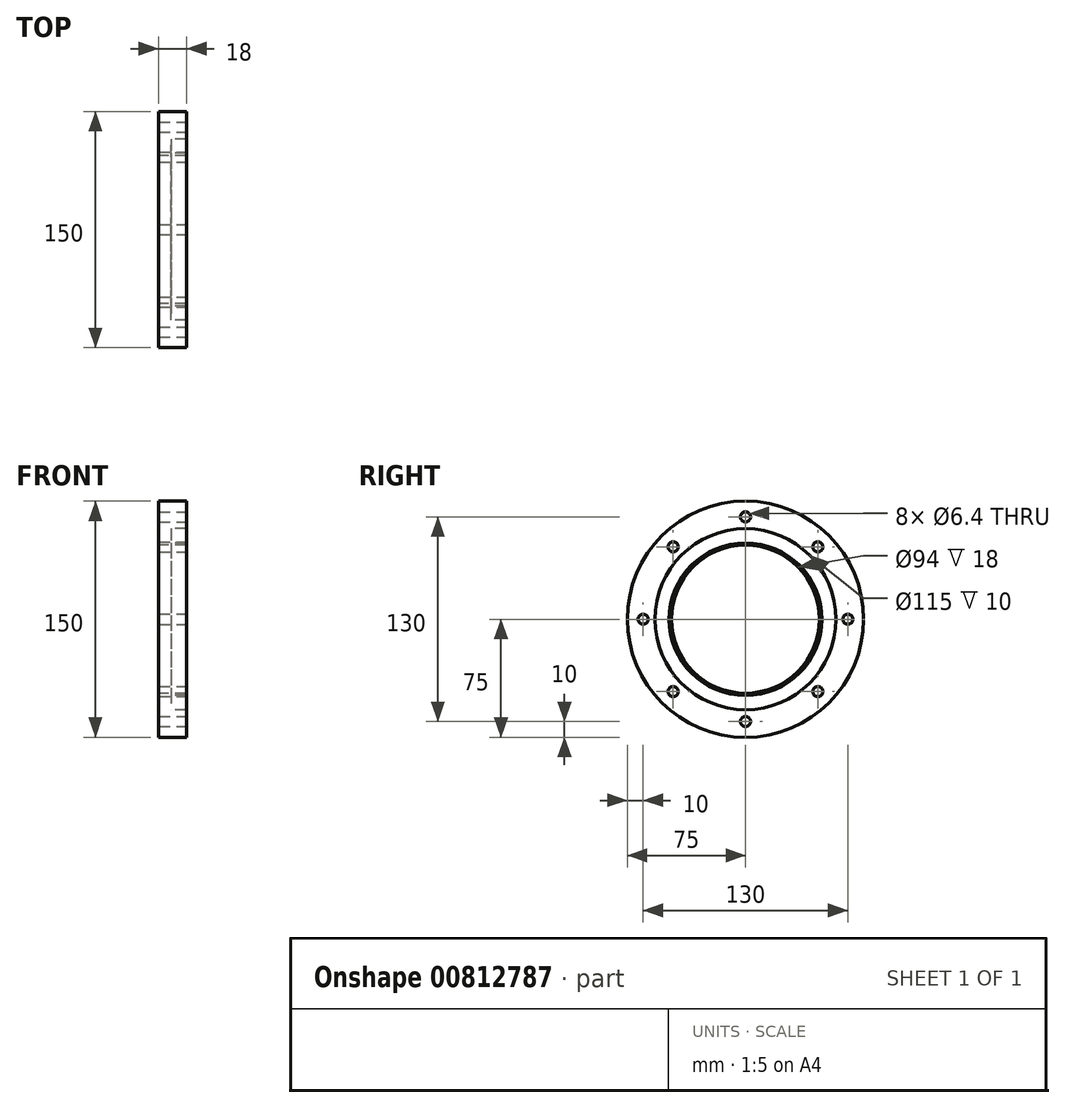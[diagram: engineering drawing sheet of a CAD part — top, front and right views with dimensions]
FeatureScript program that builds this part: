
annotation { "Feature Type Name" : "Feature", "Feature Type Description" : "" }
export const myFeature = defineFeature(function(context is Context, id is Id, definition is map)
    precondition{}
    {
        {
            assignVariable(context, id + "F0", {"name" : "meh", "anyValue" : 8});
        }
        {
            var Q0;
            Q0=qCreatedBy(makeId("Front.planeOp"),FACE);
            var sketch = newSketch(context, id + "F1", { "sketchPlane" : qUnion([Q0])});
            skLineSegment(sketch, "E0", {"start": v(0, 47) * mm, "end": v(0, 75) * mm});
            skLineSegment(sketch, "E1", {"start": v(0, 75) * mm, "end": v(18, 75) * mm});
            skLineSegment(sketch, "E2", {"start": v(18, 75) * mm, "end": v(18, 57.5) * mm});
            skLineSegment(sketch, "E3", {"start": v(18, 57.5) * mm, "end": v(8, 57.5) * mm});
            skLineSegment(sketch, "E4", {"start": v(8, 57.5) * mm, "end": v(8, 48.5) * mm});
            skLineSegment(sketch, "E5", {"start": v(8, 48.5) * mm, "end": v(18, 48.5) * mm});
            skLineSegment(sketch, "E6", {"start": v(18, 48.5) * mm, "end": v(18, 47) * mm});
            skLineSegment(sketch, "E7", {"start": v(18, 47) * mm, "end": v(0, 47) * mm});
            skLineSegment(sketch, "E8", {"start": v(0, 0) * mm, "end": v(18, 0) * mm, "construction": true});
            skSolve(sketch);
        }
        {
            var Q0;
            Q0 = qSketchRegion(id + "F1", true);
            var Q1;
            Q1=sQuery(id+"F1.wireOp",EDGE,"E8");
            revolve(context, id + "F2", {"surfaceOperationType" : NewSurfaceOperationType.NEW, "entities" : qUnion([Q0]), "axis" : qUnion([Q1]), "revolveType" : RevolveType.FULL});
        }
        {
            var Q0;
            Q0=makeQuery(id+"F2.opRevolve","SWEPT_FACE",FACE,{"disambiguationData":[OSD([sQuery(id+"F1.wireOp",EDGE,"E2")])]});
            var sketch = newSketch(context, id + "F3", { "sketchPlane" : qUnion([Q0])});
            skCircle(sketch, "E9", {"center": v(0, 65) * mm, "radius": 3.2 * mm});
            skSolve(sketch);
        }
        {
            var Q0;
            Q0 = qSketchRegion(id + "F3", true);
            var Q1;
            Q1=makeQuery(id+"F2.opRevolve","SWEPT_FACE",FACE,{"disambiguationData":[OSD([sQuery(id+"F1.wireOp",EDGE,"E0")])]});
            extrude(context, id + "F4", {"entities" : qUnion([Q0]), "endBound" : BoundingType.UP_TO_SURFACE, "oppositeDirection" : true, "depth" : 25 * mm, "endBoundEntityFace" : qUnion([Q1]), "offsetDistance" : 25 * mm});
        }
        {
            var Q0;
            Q0=makeQuery(id+"F4.opExtrude","SWEPT_BODY",BODY,{"disambiguationData":[OSD([sQuery(id+"F3.wireOp",EDGE,"E9")])]});
            var Q1;
            Q1=makeQuery(id+"F2.opRevolve","SWEPT_EDGE",EDGE,{"disambiguationData":[OSD([sQuery(id+"F1.wireOp",EDGE,"E1"),sQuery(id+"F1.wireOp",EDGE,"E2")])]});
            circularPattern(context, id + "F5", {"entities" : qUnion([Q0]), "axis" : qUnion([Q1]), "angle" : 360 * degree, "instanceCount" : getVariable(context, 'meh'), "equalSpace" : true});
        }
        {
            var Q0;
            Q0=makeQuery(id+"F4.opExtrude","SWEPT_BODY",BODY,{"disambiguationData":[OSD([sQuery(id+"F3.wireOp",EDGE,"E9")])]});
            var Q1;
            Q1=makeQuery(id+"F5.opPattern","COPY",BODY,{"derivedFrom":makeQuery(id+"F4.opExtrude","SWEPT_BODY",BODY,{"disambiguationData":[OSD([sQuery(id+"F3.wireOp",EDGE,"E9")])]}),"instanceName":"1"});
            var Q2;
            Q2=makeQuery(id+"F5.opPattern","COPY",BODY,{"derivedFrom":makeQuery(id+"F4.opExtrude","SWEPT_BODY",BODY,{"disambiguationData":[OSD([sQuery(id+"F3.wireOp",EDGE,"E9")])]}),"instanceName":"2"});
            var Q3;
            Q3=makeQuery(id+"F5.opPattern","COPY",BODY,{"derivedFrom":makeQuery(id+"F4.opExtrude","SWEPT_BODY",BODY,{"disambiguationData":[OSD([sQuery(id+"F3.wireOp",EDGE,"E9")])]}),"instanceName":"3"});
            var Q4;
            Q4=makeQuery(id+"F5.opPattern","COPY",BODY,{"derivedFrom":makeQuery(id+"F4.opExtrude","SWEPT_BODY",BODY,{"disambiguationData":[OSD([sQuery(id+"F3.wireOp",EDGE,"E9")])]}),"instanceName":"4"});
            var Q5;
            Q5=makeQuery(id+"F5.opPattern","COPY",BODY,{"derivedFrom":makeQuery(id+"F4.opExtrude","SWEPT_BODY",BODY,{"disambiguationData":[OSD([sQuery(id+"F3.wireOp",EDGE,"E9")])]}),"instanceName":"5"});
            var Q6;
            Q6=makeQuery(id+"F5.opPattern","COPY",BODY,{"derivedFrom":makeQuery(id+"F4.opExtrude","SWEPT_BODY",BODY,{"disambiguationData":[OSD([sQuery(id+"F3.wireOp",EDGE,"E9")])]}),"instanceName":"6"});
            var Q7;
            Q7=makeQuery(id+"F5.opPattern","COPY",BODY,{"derivedFrom":makeQuery(id+"F4.opExtrude","SWEPT_BODY",BODY,{"disambiguationData":[OSD([sQuery(id+"F3.wireOp",EDGE,"E9")])]}),"instanceName":"7"});
            var Q8;
            Q8=makeQuery(id+"F5.opPattern","COPY",BODY,{"derivedFrom":makeQuery(id+"F4.opExtrude","SWEPT_BODY",BODY,{"disambiguationData":[OSD([sQuery(id+"F3.wireOp",EDGE,"E9")])]}),"instanceName":"8"});
            var Q9;
            Q9=makeQuery(id+"F5.opPattern","COPY",BODY,{"derivedFrom":makeQuery(id+"F4.opExtrude","SWEPT_BODY",BODY,{"disambiguationData":[OSD([sQuery(id+"F3.wireOp",EDGE,"E9")])]}),"instanceName":"9"});
            var Q10;
            Q10=makeQuery(id+"F5.opPattern","COPY",BODY,{"derivedFrom":makeQuery(id+"F4.opExtrude","SWEPT_BODY",BODY,{"disambiguationData":[OSD([sQuery(id+"F3.wireOp",EDGE,"E9")])]}),"instanceName":"10"});
            var Q11;
            Q11=makeQuery(id+"F5.opPattern","COPY",BODY,{"derivedFrom":makeQuery(id+"F4.opExtrude","SWEPT_BODY",BODY,{"disambiguationData":[OSD([sQuery(id+"F3.wireOp",EDGE,"E9")])]}),"instanceName":"11"});
            var Q12;
            Q12=makeQuery(id+"F5.opPattern","COPY",BODY,{"derivedFrom":makeQuery(id+"F4.opExtrude","SWEPT_BODY",BODY,{"disambiguationData":[OSD([sQuery(id+"F3.wireOp",EDGE,"E9")])]}),"instanceName":"12"});
            var Q13;
            Q13=makeQuery(id+"F5.opPattern","COPY",BODY,{"derivedFrom":makeQuery(id+"F4.opExtrude","SWEPT_BODY",BODY,{"disambiguationData":[OSD([sQuery(id+"F3.wireOp",EDGE,"E9")])]}),"instanceName":"13"});
            var Q14;
            Q14=makeQuery(id+"F5.opPattern","COPY",BODY,{"derivedFrom":makeQuery(id+"F4.opExtrude","SWEPT_BODY",BODY,{"disambiguationData":[OSD([sQuery(id+"F3.wireOp",EDGE,"E9")])]}),"instanceName":"14"});
            var Q15;
            Q15=makeQuery(id+"F5.opPattern","COPY",BODY,{"derivedFrom":makeQuery(id+"F4.opExtrude","SWEPT_BODY",BODY,{"disambiguationData":[OSD([sQuery(id+"F3.wireOp",EDGE,"E9")])]}),"instanceName":"15"});
            var Q16;
            Q16=makeQuery(id+"F5.opPattern","COPY",BODY,{"derivedFrom":makeQuery(id+"F4.opExtrude","SWEPT_BODY",BODY,{"disambiguationData":[OSD([sQuery(id+"F3.wireOp",EDGE,"E9")])]}),"instanceName":"16"});
            var Q17;
            Q17=makeQuery(id+"F5.opPattern","COPY",BODY,{"derivedFrom":makeQuery(id+"F4.opExtrude","SWEPT_BODY",BODY,{"disambiguationData":[OSD([sQuery(id+"F3.wireOp",EDGE,"E9")])]}),"instanceName":"17"});
            var Q18;
            Q18=makeQuery(id+"F5.opPattern","COPY",BODY,{"derivedFrom":makeQuery(id+"F4.opExtrude","SWEPT_BODY",BODY,{"disambiguationData":[OSD([sQuery(id+"F3.wireOp",EDGE,"E9")])]}),"instanceName":"18"});
            var Q19;
            Q19=makeQuery(id+"F5.opPattern","COPY",BODY,{"derivedFrom":makeQuery(id+"F4.opExtrude","SWEPT_BODY",BODY,{"disambiguationData":[OSD([sQuery(id+"F3.wireOp",EDGE,"E9")])]}),"instanceName":"19"});
            var Q20;
            Q20=makeQuery(id+"F5.opPattern","COPY",BODY,{"derivedFrom":makeQuery(id+"F4.opExtrude","SWEPT_BODY",BODY,{"disambiguationData":[OSD([sQuery(id+"F3.wireOp",EDGE,"E9")])]}),"instanceName":"20"});
            var Q21;
            Q21=makeQuery(id+"F5.opPattern","COPY",BODY,{"derivedFrom":makeQuery(id+"F4.opExtrude","SWEPT_BODY",BODY,{"disambiguationData":[OSD([sQuery(id+"F3.wireOp",EDGE,"E9")])]}),"instanceName":"21"});
            var Q22;
            Q22=makeQuery(id+"F5.opPattern","COPY",BODY,{"derivedFrom":makeQuery(id+"F4.opExtrude","SWEPT_BODY",BODY,{"disambiguationData":[OSD([sQuery(id+"F3.wireOp",EDGE,"E9")])]}),"instanceName":"22"});
            var Q23;
            Q23=makeQuery(id+"F5.opPattern","COPY",BODY,{"derivedFrom":makeQuery(id+"F4.opExtrude","SWEPT_BODY",BODY,{"disambiguationData":[OSD([sQuery(id+"F3.wireOp",EDGE,"E9")])]}),"instanceName":"23"});
            var Q24;
            Q24=makeQuery(id+"F5.opPattern","COPY",BODY,{"derivedFrom":makeQuery(id+"F4.opExtrude","SWEPT_BODY",BODY,{"disambiguationData":[OSD([sQuery(id+"F3.wireOp",EDGE,"E9")])]}),"instanceName":"24"});
            var Q25;
            Q25=makeQuery(id+"F5.opPattern","COPY",BODY,{"derivedFrom":makeQuery(id+"F4.opExtrude","SWEPT_BODY",BODY,{"disambiguationData":[OSD([sQuery(id+"F3.wireOp",EDGE,"E9")])]}),"instanceName":"25"});
            var Q26;
            Q26=makeQuery(id+"F5.opPattern","COPY",BODY,{"derivedFrom":makeQuery(id+"F4.opExtrude","SWEPT_BODY",BODY,{"disambiguationData":[OSD([sQuery(id+"F3.wireOp",EDGE,"E9")])]}),"instanceName":"26"});
            var Q27;
            Q27=makeQuery(id+"F5.opPattern","COPY",BODY,{"derivedFrom":makeQuery(id+"F4.opExtrude","SWEPT_BODY",BODY,{"disambiguationData":[OSD([sQuery(id+"F3.wireOp",EDGE,"E9")])]}),"instanceName":"27"});
            var Q28;
            Q28=makeQuery(id+"F5.opPattern","COPY",BODY,{"derivedFrom":makeQuery(id+"F4.opExtrude","SWEPT_BODY",BODY,{"disambiguationData":[OSD([sQuery(id+"F3.wireOp",EDGE,"E9")])]}),"instanceName":"28"});
            var Q29;
            Q29=makeQuery(id+"F5.opPattern","COPY",BODY,{"derivedFrom":makeQuery(id+"F4.opExtrude","SWEPT_BODY",BODY,{"disambiguationData":[OSD([sQuery(id+"F3.wireOp",EDGE,"E9")])]}),"instanceName":"29"});
            var Q30;
            Q30=makeQuery(id+"F5.opPattern","COPY",BODY,{"derivedFrom":makeQuery(id+"F4.opExtrude","SWEPT_BODY",BODY,{"disambiguationData":[OSD([sQuery(id+"F3.wireOp",EDGE,"E9")])]}),"instanceName":"30"});
            var Q31;
            Q31=makeQuery(id+"F5.opPattern","COPY",BODY,{"derivedFrom":makeQuery(id+"F4.opExtrude","SWEPT_BODY",BODY,{"disambiguationData":[OSD([sQuery(id+"F3.wireOp",EDGE,"E9")])]}),"instanceName":"31"});
            var Q32;
            Q32=makeQuery(id+"F5.opPattern","COPY",BODY,{"derivedFrom":makeQuery(id+"F4.opExtrude","SWEPT_BODY",BODY,{"disambiguationData":[OSD([sQuery(id+"F3.wireOp",EDGE,"E9")])]}),"instanceName":"32"});
            var Q33;
            Q33=makeQuery(id+"F5.opPattern","COPY",BODY,{"derivedFrom":makeQuery(id+"F4.opExtrude","SWEPT_BODY",BODY,{"disambiguationData":[OSD([sQuery(id+"F3.wireOp",EDGE,"E9")])]}),"instanceName":"33"});
            var Q34;
            Q34=makeQuery(id+"F5.opPattern","COPY",BODY,{"derivedFrom":makeQuery(id+"F4.opExtrude","SWEPT_BODY",BODY,{"disambiguationData":[OSD([sQuery(id+"F3.wireOp",EDGE,"E9")])]}),"instanceName":"34"});
            var Q35;
            Q35=makeQuery(id+"F5.opPattern","COPY",BODY,{"derivedFrom":makeQuery(id+"F4.opExtrude","SWEPT_BODY",BODY,{"disambiguationData":[OSD([sQuery(id+"F3.wireOp",EDGE,"E9")])]}),"instanceName":"35"});
            var Q36;
            Q36=makeQuery(id+"F5.opPattern","COPY",BODY,{"derivedFrom":makeQuery(id+"F4.opExtrude","SWEPT_BODY",BODY,{"disambiguationData":[OSD([sQuery(id+"F3.wireOp",EDGE,"E9")])]}),"instanceName":"36"});
            var Q37;
            Q37=makeQuery(id+"F5.opPattern","COPY",BODY,{"derivedFrom":makeQuery(id+"F4.opExtrude","SWEPT_BODY",BODY,{"disambiguationData":[OSD([sQuery(id+"F3.wireOp",EDGE,"E9")])]}),"instanceName":"37"});
            var Q38;
            Q38=makeQuery(id+"F5.opPattern","COPY",BODY,{"derivedFrom":makeQuery(id+"F4.opExtrude","SWEPT_BODY",BODY,{"disambiguationData":[OSD([sQuery(id+"F3.wireOp",EDGE,"E9")])]}),"instanceName":"38"});
            var Q39;
            Q39=makeQuery(id+"F5.opPattern","COPY",BODY,{"derivedFrom":makeQuery(id+"F4.opExtrude","SWEPT_BODY",BODY,{"disambiguationData":[OSD([sQuery(id+"F3.wireOp",EDGE,"E9")])]}),"instanceName":"39"});
            var Q40;
            Q40=makeQuery(id+"F5.opPattern","COPY",BODY,{"derivedFrom":makeQuery(id+"F4.opExtrude","SWEPT_BODY",BODY,{"disambiguationData":[OSD([sQuery(id+"F3.wireOp",EDGE,"E9")])]}),"instanceName":"40"});
            var Q41;
            Q41=makeQuery(id+"F5.opPattern","COPY",BODY,{"derivedFrom":makeQuery(id+"F4.opExtrude","SWEPT_BODY",BODY,{"disambiguationData":[OSD([sQuery(id+"F3.wireOp",EDGE,"E9")])]}),"instanceName":"41"});
            var Q42;
            Q42=makeQuery(id+"F5.opPattern","COPY",BODY,{"derivedFrom":makeQuery(id+"F4.opExtrude","SWEPT_BODY",BODY,{"disambiguationData":[OSD([sQuery(id+"F3.wireOp",EDGE,"E9")])]}),"instanceName":"42"});
            var Q43;
            Q43=makeQuery(id+"F5.opPattern","COPY",BODY,{"derivedFrom":makeQuery(id+"F4.opExtrude","SWEPT_BODY",BODY,{"disambiguationData":[OSD([sQuery(id+"F3.wireOp",EDGE,"E9")])]}),"instanceName":"43"});
            var Q44;
            Q44=makeQuery(id+"F5.opPattern","COPY",BODY,{"derivedFrom":makeQuery(id+"F4.opExtrude","SWEPT_BODY",BODY,{"disambiguationData":[OSD([sQuery(id+"F3.wireOp",EDGE,"E9")])]}),"instanceName":"44"});
            var Q45;
            Q45=makeQuery(id+"F5.opPattern","COPY",BODY,{"derivedFrom":makeQuery(id+"F4.opExtrude","SWEPT_BODY",BODY,{"disambiguationData":[OSD([sQuery(id+"F3.wireOp",EDGE,"E9")])]}),"instanceName":"45"});
            var Q46;
            Q46=makeQuery(id+"F5.opPattern","COPY",BODY,{"derivedFrom":makeQuery(id+"F4.opExtrude","SWEPT_BODY",BODY,{"disambiguationData":[OSD([sQuery(id+"F3.wireOp",EDGE,"E9")])]}),"instanceName":"46"});
            var Q47;
            Q47=makeQuery(id+"F5.opPattern","COPY",BODY,{"derivedFrom":makeQuery(id+"F4.opExtrude","SWEPT_BODY",BODY,{"disambiguationData":[OSD([sQuery(id+"F3.wireOp",EDGE,"E9")])]}),"instanceName":"47"});
            var Q48;
            Q48=makeQuery(id+"F5.opPattern","COPY",BODY,{"derivedFrom":makeQuery(id+"F4.opExtrude","SWEPT_BODY",BODY,{"disambiguationData":[OSD([sQuery(id+"F3.wireOp",EDGE,"E9")])]}),"instanceName":"48"});
            var Q49;
            Q49=makeQuery(id+"F5.opPattern","COPY",BODY,{"derivedFrom":makeQuery(id+"F4.opExtrude","SWEPT_BODY",BODY,{"disambiguationData":[OSD([sQuery(id+"F3.wireOp",EDGE,"E9")])]}),"instanceName":"49"});
            var Q50;
            Q50=makeQuery(id+"F5.opPattern","COPY",BODY,{"derivedFrom":makeQuery(id+"F4.opExtrude","SWEPT_BODY",BODY,{"disambiguationData":[OSD([sQuery(id+"F3.wireOp",EDGE,"E9")])]}),"instanceName":"50"});
            var Q51;
            Q51=makeQuery(id+"F5.opPattern","COPY",BODY,{"derivedFrom":makeQuery(id+"F4.opExtrude","SWEPT_BODY",BODY,{"disambiguationData":[OSD([sQuery(id+"F3.wireOp",EDGE,"E9")])]}),"instanceName":"51"});
            var Q52;
            Q52=makeQuery(id+"F5.opPattern","COPY",BODY,{"derivedFrom":makeQuery(id+"F4.opExtrude","SWEPT_BODY",BODY,{"disambiguationData":[OSD([sQuery(id+"F3.wireOp",EDGE,"E9")])]}),"instanceName":"52"});
            var Q53;
            Q53=makeQuery(id+"F5.opPattern","COPY",BODY,{"derivedFrom":makeQuery(id+"F4.opExtrude","SWEPT_BODY",BODY,{"disambiguationData":[OSD([sQuery(id+"F3.wireOp",EDGE,"E9")])]}),"instanceName":"53"});
            var Q54;
            Q54=makeQuery(id+"F5.opPattern","COPY",BODY,{"derivedFrom":makeQuery(id+"F4.opExtrude","SWEPT_BODY",BODY,{"disambiguationData":[OSD([sQuery(id+"F3.wireOp",EDGE,"E9")])]}),"instanceName":"54"});
            var Q55;
            Q55=makeQuery(id+"F5.opPattern","COPY",BODY,{"derivedFrom":makeQuery(id+"F4.opExtrude","SWEPT_BODY",BODY,{"disambiguationData":[OSD([sQuery(id+"F3.wireOp",EDGE,"E9")])]}),"instanceName":"55"});
            var Q56;
            Q56=makeQuery(id+"F5.opPattern","COPY",BODY,{"derivedFrom":makeQuery(id+"F4.opExtrude","SWEPT_BODY",BODY,{"disambiguationData":[OSD([sQuery(id+"F3.wireOp",EDGE,"E9")])]}),"instanceName":"56"});
            var Q57;
            Q57=makeQuery(id+"F5.opPattern","COPY",BODY,{"derivedFrom":makeQuery(id+"F4.opExtrude","SWEPT_BODY",BODY,{"disambiguationData":[OSD([sQuery(id+"F3.wireOp",EDGE,"E9")])]}),"instanceName":"57"});
            var Q58;
            Q58=makeQuery(id+"F5.opPattern","COPY",BODY,{"derivedFrom":makeQuery(id+"F4.opExtrude","SWEPT_BODY",BODY,{"disambiguationData":[OSD([sQuery(id+"F3.wireOp",EDGE,"E9")])]}),"instanceName":"58"});
            var Q59;
            Q59=makeQuery(id+"F5.opPattern","COPY",BODY,{"derivedFrom":makeQuery(id+"F4.opExtrude","SWEPT_BODY",BODY,{"disambiguationData":[OSD([sQuery(id+"F3.wireOp",EDGE,"E9")])]}),"instanceName":"59"});
            var Q60;
            Q60=makeQuery(id+"F5.opPattern","COPY",BODY,{"derivedFrom":makeQuery(id+"F4.opExtrude","SWEPT_BODY",BODY,{"disambiguationData":[OSD([sQuery(id+"F3.wireOp",EDGE,"E9")])]}),"instanceName":"60"});
            var Q61;
            Q61=makeQuery(id+"F5.opPattern","COPY",BODY,{"derivedFrom":makeQuery(id+"F4.opExtrude","SWEPT_BODY",BODY,{"disambiguationData":[OSD([sQuery(id+"F3.wireOp",EDGE,"E9")])]}),"instanceName":"61"});
            var Q62;
            Q62=makeQuery(id+"F5.opPattern","COPY",BODY,{"derivedFrom":makeQuery(id+"F4.opExtrude","SWEPT_BODY",BODY,{"disambiguationData":[OSD([sQuery(id+"F3.wireOp",EDGE,"E9")])]}),"instanceName":"62"});
            var Q63;
            Q63=makeQuery(id+"F5.opPattern","COPY",BODY,{"derivedFrom":makeQuery(id+"F4.opExtrude","SWEPT_BODY",BODY,{"disambiguationData":[OSD([sQuery(id+"F3.wireOp",EDGE,"E9")])]}),"instanceName":"63"});
            var Q64;
            Q64=makeQuery(id+"F5.opPattern","COPY",BODY,{"derivedFrom":makeQuery(id+"F4.opExtrude","SWEPT_BODY",BODY,{"disambiguationData":[OSD([sQuery(id+"F3.wireOp",EDGE,"E9")])]}),"instanceName":"64"});
            var Q65;
            Q65=makeQuery(id+"F5.opPattern","COPY",BODY,{"derivedFrom":makeQuery(id+"F4.opExtrude","SWEPT_BODY",BODY,{"disambiguationData":[OSD([sQuery(id+"F3.wireOp",EDGE,"E9")])]}),"instanceName":"65"});
            var Q66;
            Q66=makeQuery(id+"F5.opPattern","COPY",BODY,{"derivedFrom":makeQuery(id+"F4.opExtrude","SWEPT_BODY",BODY,{"disambiguationData":[OSD([sQuery(id+"F3.wireOp",EDGE,"E9")])]}),"instanceName":"66"});
            var Q67;
            Q67=makeQuery(id+"F5.opPattern","COPY",BODY,{"derivedFrom":makeQuery(id+"F4.opExtrude","SWEPT_BODY",BODY,{"disambiguationData":[OSD([sQuery(id+"F3.wireOp",EDGE,"E9")])]}),"instanceName":"67"});
            var Q68;
            Q68=makeQuery(id+"F5.opPattern","COPY",BODY,{"derivedFrom":makeQuery(id+"F4.opExtrude","SWEPT_BODY",BODY,{"disambiguationData":[OSD([sQuery(id+"F3.wireOp",EDGE,"E9")])]}),"instanceName":"68"});
            var Q69;
            Q69=makeQuery(id+"F5.opPattern","COPY",BODY,{"derivedFrom":makeQuery(id+"F4.opExtrude","SWEPT_BODY",BODY,{"disambiguationData":[OSD([sQuery(id+"F3.wireOp",EDGE,"E9")])]}),"instanceName":"69"});
            var Q70;
            Q70=makeQuery(id+"F5.opPattern","COPY",BODY,{"derivedFrom":makeQuery(id+"F4.opExtrude","SWEPT_BODY",BODY,{"disambiguationData":[OSD([sQuery(id+"F3.wireOp",EDGE,"E9")])]}),"instanceName":"70"});
            var Q71;
            Q71=makeQuery(id+"F5.opPattern","COPY",BODY,{"derivedFrom":makeQuery(id+"F4.opExtrude","SWEPT_BODY",BODY,{"disambiguationData":[OSD([sQuery(id+"F3.wireOp",EDGE,"E9")])]}),"instanceName":"71"});
            var Q72;
            Q72=makeQuery(id+"F5.opPattern","COPY",BODY,{"derivedFrom":makeQuery(id+"F4.opExtrude","SWEPT_BODY",BODY,{"disambiguationData":[OSD([sQuery(id+"F3.wireOp",EDGE,"E9")])]}),"instanceName":"72"});
            var Q73;
            Q73=makeQuery(id+"F5.opPattern","COPY",BODY,{"derivedFrom":makeQuery(id+"F4.opExtrude","SWEPT_BODY",BODY,{"disambiguationData":[OSD([sQuery(id+"F3.wireOp",EDGE,"E9")])]}),"instanceName":"73"});
            var Q74;
            Q74=makeQuery(id+"F5.opPattern","COPY",BODY,{"derivedFrom":makeQuery(id+"F4.opExtrude","SWEPT_BODY",BODY,{"disambiguationData":[OSD([sQuery(id+"F3.wireOp",EDGE,"E9")])]}),"instanceName":"74"});
            var Q75;
            Q75=makeQuery(id+"F5.opPattern","COPY",BODY,{"derivedFrom":makeQuery(id+"F4.opExtrude","SWEPT_BODY",BODY,{"disambiguationData":[OSD([sQuery(id+"F3.wireOp",EDGE,"E9")])]}),"instanceName":"75"});
            var Q76;
            Q76=makeQuery(id+"F5.opPattern","COPY",BODY,{"derivedFrom":makeQuery(id+"F4.opExtrude","SWEPT_BODY",BODY,{"disambiguationData":[OSD([sQuery(id+"F3.wireOp",EDGE,"E9")])]}),"instanceName":"76"});
            var Q77;
            Q77=makeQuery(id+"F5.opPattern","COPY",BODY,{"derivedFrom":makeQuery(id+"F4.opExtrude","SWEPT_BODY",BODY,{"disambiguationData":[OSD([sQuery(id+"F3.wireOp",EDGE,"E9")])]}),"instanceName":"77"});
            var Q78;
            Q78=makeQuery(id+"F5.opPattern","COPY",BODY,{"derivedFrom":makeQuery(id+"F4.opExtrude","SWEPT_BODY",BODY,{"disambiguationData":[OSD([sQuery(id+"F3.wireOp",EDGE,"E9")])]}),"instanceName":"78"});
            var Q79;
            Q79=makeQuery(id+"F5.opPattern","COPY",BODY,{"derivedFrom":makeQuery(id+"F4.opExtrude","SWEPT_BODY",BODY,{"disambiguationData":[OSD([sQuery(id+"F3.wireOp",EDGE,"E9")])]}),"instanceName":"79"});
            var Q80;
            Q80=makeQuery(id+"F5.opPattern","COPY",BODY,{"derivedFrom":makeQuery(id+"F4.opExtrude","SWEPT_BODY",BODY,{"disambiguationData":[OSD([sQuery(id+"F3.wireOp",EDGE,"E9")])]}),"instanceName":"80"});
            var Q81;
            Q81=makeQuery(id+"F5.opPattern","COPY",BODY,{"derivedFrom":makeQuery(id+"F4.opExtrude","SWEPT_BODY",BODY,{"disambiguationData":[OSD([sQuery(id+"F3.wireOp",EDGE,"E9")])]}),"instanceName":"81"});
            var Q82;
            Q82=makeQuery(id+"F5.opPattern","COPY",BODY,{"derivedFrom":makeQuery(id+"F4.opExtrude","SWEPT_BODY",BODY,{"disambiguationData":[OSD([sQuery(id+"F3.wireOp",EDGE,"E9")])]}),"instanceName":"82"});
            var Q83;
            Q83=makeQuery(id+"F5.opPattern","COPY",BODY,{"derivedFrom":makeQuery(id+"F4.opExtrude","SWEPT_BODY",BODY,{"disambiguationData":[OSD([sQuery(id+"F3.wireOp",EDGE,"E9")])]}),"instanceName":"83"});
            var Q84;
            Q84=makeQuery(id+"F5.opPattern","COPY",BODY,{"derivedFrom":makeQuery(id+"F4.opExtrude","SWEPT_BODY",BODY,{"disambiguationData":[OSD([sQuery(id+"F3.wireOp",EDGE,"E9")])]}),"instanceName":"84"});
            var Q85;
            Q85=makeQuery(id+"F5.opPattern","COPY",BODY,{"derivedFrom":makeQuery(id+"F4.opExtrude","SWEPT_BODY",BODY,{"disambiguationData":[OSD([sQuery(id+"F3.wireOp",EDGE,"E9")])]}),"instanceName":"85"});
            var Q86;
            Q86=makeQuery(id+"F5.opPattern","COPY",BODY,{"derivedFrom":makeQuery(id+"F4.opExtrude","SWEPT_BODY",BODY,{"disambiguationData":[OSD([sQuery(id+"F3.wireOp",EDGE,"E9")])]}),"instanceName":"86"});
            var Q87;
            Q87=makeQuery(id+"F5.opPattern","COPY",BODY,{"derivedFrom":makeQuery(id+"F4.opExtrude","SWEPT_BODY",BODY,{"disambiguationData":[OSD([sQuery(id+"F3.wireOp",EDGE,"E9")])]}),"instanceName":"87"});
            var Q88;
            Q88=makeQuery(id+"F5.opPattern","COPY",BODY,{"derivedFrom":makeQuery(id+"F4.opExtrude","SWEPT_BODY",BODY,{"disambiguationData":[OSD([sQuery(id+"F3.wireOp",EDGE,"E9")])]}),"instanceName":"88"});
            var Q89;
            Q89=makeQuery(id+"F5.opPattern","COPY",BODY,{"derivedFrom":makeQuery(id+"F4.opExtrude","SWEPT_BODY",BODY,{"disambiguationData":[OSD([sQuery(id+"F3.wireOp",EDGE,"E9")])]}),"instanceName":"89"});
            var Q90;
            Q90=makeQuery(id+"F5.opPattern","COPY",BODY,{"derivedFrom":makeQuery(id+"F4.opExtrude","SWEPT_BODY",BODY,{"disambiguationData":[OSD([sQuery(id+"F3.wireOp",EDGE,"E9")])]}),"instanceName":"90"});
            var Q91;
            Q91=makeQuery(id+"F5.opPattern","COPY",BODY,{"derivedFrom":makeQuery(id+"F4.opExtrude","SWEPT_BODY",BODY,{"disambiguationData":[OSD([sQuery(id+"F3.wireOp",EDGE,"E9")])]}),"instanceName":"91"});
            var Q92;
            Q92=makeQuery(id+"F5.opPattern","COPY",BODY,{"derivedFrom":makeQuery(id+"F4.opExtrude","SWEPT_BODY",BODY,{"disambiguationData":[OSD([sQuery(id+"F3.wireOp",EDGE,"E9")])]}),"instanceName":"92"});
            var Q93;
            Q93=makeQuery(id+"F5.opPattern","COPY",BODY,{"derivedFrom":makeQuery(id+"F4.opExtrude","SWEPT_BODY",BODY,{"disambiguationData":[OSD([sQuery(id+"F3.wireOp",EDGE,"E9")])]}),"instanceName":"93"});
            var Q94;
            Q94=makeQuery(id+"F5.opPattern","COPY",BODY,{"derivedFrom":makeQuery(id+"F4.opExtrude","SWEPT_BODY",BODY,{"disambiguationData":[OSD([sQuery(id+"F3.wireOp",EDGE,"E9")])]}),"instanceName":"94"});
            var Q95;
            Q95=makeQuery(id+"F5.opPattern","COPY",BODY,{"derivedFrom":makeQuery(id+"F4.opExtrude","SWEPT_BODY",BODY,{"disambiguationData":[OSD([sQuery(id+"F3.wireOp",EDGE,"E9")])]}),"instanceName":"95"});
            var Q96;
            Q96=makeQuery(id+"F5.opPattern","COPY",BODY,{"derivedFrom":makeQuery(id+"F4.opExtrude","SWEPT_BODY",BODY,{"disambiguationData":[OSD([sQuery(id+"F3.wireOp",EDGE,"E9")])]}),"instanceName":"96"});
            var Q97;
            Q97=makeQuery(id+"F5.opPattern","COPY",BODY,{"derivedFrom":makeQuery(id+"F4.opExtrude","SWEPT_BODY",BODY,{"disambiguationData":[OSD([sQuery(id+"F3.wireOp",EDGE,"E9")])]}),"instanceName":"97"});
            var Q98;
            Q98=makeQuery(id+"F5.opPattern","COPY",BODY,{"derivedFrom":makeQuery(id+"F4.opExtrude","SWEPT_BODY",BODY,{"disambiguationData":[OSD([sQuery(id+"F3.wireOp",EDGE,"E9")])]}),"instanceName":"98"});
            var Q99;
            Q99=makeQuery(id+"F5.opPattern","COPY",BODY,{"derivedFrom":makeQuery(id+"F4.opExtrude","SWEPT_BODY",BODY,{"disambiguationData":[OSD([sQuery(id+"F3.wireOp",EDGE,"E9")])]}),"instanceName":"99"});
            var Q100;
            Q100=makeQuery(id+"F5.opPattern","COPY",BODY,{"derivedFrom":makeQuery(id+"F4.opExtrude","SWEPT_BODY",BODY,{"disambiguationData":[OSD([sQuery(id+"F3.wireOp",EDGE,"E9")])]}),"instanceName":"100"});
            var Q101;
            Q101=makeQuery(id+"F5.opPattern","COPY",BODY,{"derivedFrom":makeQuery(id+"F4.opExtrude","SWEPT_BODY",BODY,{"disambiguationData":[OSD([sQuery(id+"F3.wireOp",EDGE,"E9")])]}),"instanceName":"101"});
            var Q102;
            Q102=makeQuery(id+"F5.opPattern","COPY",BODY,{"derivedFrom":makeQuery(id+"F4.opExtrude","SWEPT_BODY",BODY,{"disambiguationData":[OSD([sQuery(id+"F3.wireOp",EDGE,"E9")])]}),"instanceName":"102"});
            var Q103;
            Q103=makeQuery(id+"F5.opPattern","COPY",BODY,{"derivedFrom":makeQuery(id+"F4.opExtrude","SWEPT_BODY",BODY,{"disambiguationData":[OSD([sQuery(id+"F3.wireOp",EDGE,"E9")])]}),"instanceName":"103"});
            var Q104;
            Q104=makeQuery(id+"F5.opPattern","COPY",BODY,{"derivedFrom":makeQuery(id+"F4.opExtrude","SWEPT_BODY",BODY,{"disambiguationData":[OSD([sQuery(id+"F3.wireOp",EDGE,"E9")])]}),"instanceName":"104"});
            var Q105;
            Q105=makeQuery(id+"F5.opPattern","COPY",BODY,{"derivedFrom":makeQuery(id+"F4.opExtrude","SWEPT_BODY",BODY,{"disambiguationData":[OSD([sQuery(id+"F3.wireOp",EDGE,"E9")])]}),"instanceName":"105"});
            var Q106;
            Q106=makeQuery(id+"F5.opPattern","COPY",BODY,{"derivedFrom":makeQuery(id+"F4.opExtrude","SWEPT_BODY",BODY,{"disambiguationData":[OSD([sQuery(id+"F3.wireOp",EDGE,"E9")])]}),"instanceName":"106"});
            var Q107;
            Q107=makeQuery(id+"F5.opPattern","COPY",BODY,{"derivedFrom":makeQuery(id+"F4.opExtrude","SWEPT_BODY",BODY,{"disambiguationData":[OSD([sQuery(id+"F3.wireOp",EDGE,"E9")])]}),"instanceName":"107"});
            var Q108;
            Q108=makeQuery(id+"F5.opPattern","COPY",BODY,{"derivedFrom":makeQuery(id+"F4.opExtrude","SWEPT_BODY",BODY,{"disambiguationData":[OSD([sQuery(id+"F3.wireOp",EDGE,"E9")])]}),"instanceName":"108"});
            var Q109;
            Q109=makeQuery(id+"F5.opPattern","COPY",BODY,{"derivedFrom":makeQuery(id+"F4.opExtrude","SWEPT_BODY",BODY,{"disambiguationData":[OSD([sQuery(id+"F3.wireOp",EDGE,"E9")])]}),"instanceName":"109"});
            var Q110;
            Q110=makeQuery(id+"F5.opPattern","COPY",BODY,{"derivedFrom":makeQuery(id+"F4.opExtrude","SWEPT_BODY",BODY,{"disambiguationData":[OSD([sQuery(id+"F3.wireOp",EDGE,"E9")])]}),"instanceName":"110"});
            var Q111;
            Q111=makeQuery(id+"F5.opPattern","COPY",BODY,{"derivedFrom":makeQuery(id+"F4.opExtrude","SWEPT_BODY",BODY,{"disambiguationData":[OSD([sQuery(id+"F3.wireOp",EDGE,"E9")])]}),"instanceName":"111"});
            var Q112;
            Q112=makeQuery(id+"F5.opPattern","COPY",BODY,{"derivedFrom":makeQuery(id+"F4.opExtrude","SWEPT_BODY",BODY,{"disambiguationData":[OSD([sQuery(id+"F3.wireOp",EDGE,"E9")])]}),"instanceName":"112"});
            var Q113;
            Q113=makeQuery(id+"F5.opPattern","COPY",BODY,{"derivedFrom":makeQuery(id+"F4.opExtrude","SWEPT_BODY",BODY,{"disambiguationData":[OSD([sQuery(id+"F3.wireOp",EDGE,"E9")])]}),"instanceName":"113"});
            var Q114;
            Q114=makeQuery(id+"F5.opPattern","COPY",BODY,{"derivedFrom":makeQuery(id+"F4.opExtrude","SWEPT_BODY",BODY,{"disambiguationData":[OSD([sQuery(id+"F3.wireOp",EDGE,"E9")])]}),"instanceName":"114"});
            var Q115;
            Q115=makeQuery(id+"F5.opPattern","COPY",BODY,{"derivedFrom":makeQuery(id+"F4.opExtrude","SWEPT_BODY",BODY,{"disambiguationData":[OSD([sQuery(id+"F3.wireOp",EDGE,"E9")])]}),"instanceName":"115"});
            var Q116;
            Q116=makeQuery(id+"F5.opPattern","COPY",BODY,{"derivedFrom":makeQuery(id+"F4.opExtrude","SWEPT_BODY",BODY,{"disambiguationData":[OSD([sQuery(id+"F3.wireOp",EDGE,"E9")])]}),"instanceName":"116"});
            var Q117;
            Q117=makeQuery(id+"F5.opPattern","COPY",BODY,{"derivedFrom":makeQuery(id+"F4.opExtrude","SWEPT_BODY",BODY,{"disambiguationData":[OSD([sQuery(id+"F3.wireOp",EDGE,"E9")])]}),"instanceName":"117"});
            var Q118;
            Q118=makeQuery(id+"F5.opPattern","COPY",BODY,{"derivedFrom":makeQuery(id+"F4.opExtrude","SWEPT_BODY",BODY,{"disambiguationData":[OSD([sQuery(id+"F3.wireOp",EDGE,"E9")])]}),"instanceName":"118"});
            var Q119;
            Q119=makeQuery(id+"F5.opPattern","COPY",BODY,{"derivedFrom":makeQuery(id+"F4.opExtrude","SWEPT_BODY",BODY,{"disambiguationData":[OSD([sQuery(id+"F3.wireOp",EDGE,"E9")])]}),"instanceName":"119"});
            var Q120;
            Q120=makeQuery(id+"F5.opPattern","COPY",BODY,{"derivedFrom":makeQuery(id+"F4.opExtrude","SWEPT_BODY",BODY,{"disambiguationData":[OSD([sQuery(id+"F3.wireOp",EDGE,"E9")])]}),"instanceName":"120"});
            var Q121;
            Q121=makeQuery(id+"F5.opPattern","COPY",BODY,{"derivedFrom":makeQuery(id+"F4.opExtrude","SWEPT_BODY",BODY,{"disambiguationData":[OSD([sQuery(id+"F3.wireOp",EDGE,"E9")])]}),"instanceName":"121"});
            var Q122;
            Q122=makeQuery(id+"F5.opPattern","COPY",BODY,{"derivedFrom":makeQuery(id+"F4.opExtrude","SWEPT_BODY",BODY,{"disambiguationData":[OSD([sQuery(id+"F3.wireOp",EDGE,"E9")])]}),"instanceName":"122"});
            var Q123;
            Q123=makeQuery(id+"F5.opPattern","COPY",BODY,{"derivedFrom":makeQuery(id+"F4.opExtrude","SWEPT_BODY",BODY,{"disambiguationData":[OSD([sQuery(id+"F3.wireOp",EDGE,"E9")])]}),"instanceName":"123"});
            var Q124;
            Q124=makeQuery(id+"F5.opPattern","COPY",BODY,{"derivedFrom":makeQuery(id+"F4.opExtrude","SWEPT_BODY",BODY,{"disambiguationData":[OSD([sQuery(id+"F3.wireOp",EDGE,"E9")])]}),"instanceName":"124"});
            var Q125;
            Q125=makeQuery(id+"F5.opPattern","COPY",BODY,{"derivedFrom":makeQuery(id+"F4.opExtrude","SWEPT_BODY",BODY,{"disambiguationData":[OSD([sQuery(id+"F3.wireOp",EDGE,"E9")])]}),"instanceName":"125"});
            var Q126;
            Q126=makeQuery(id+"F5.opPattern","COPY",BODY,{"derivedFrom":makeQuery(id+"F4.opExtrude","SWEPT_BODY",BODY,{"disambiguationData":[OSD([sQuery(id+"F3.wireOp",EDGE,"E9")])]}),"instanceName":"126"});
            var Q127;
            Q127=makeQuery(id+"F5.opPattern","COPY",BODY,{"derivedFrom":makeQuery(id+"F4.opExtrude","SWEPT_BODY",BODY,{"disambiguationData":[OSD([sQuery(id+"F3.wireOp",EDGE,"E9")])]}),"instanceName":"127"});
            var Q128;
            Q128=makeQuery(id+"F5.opPattern","COPY",BODY,{"derivedFrom":makeQuery(id+"F4.opExtrude","SWEPT_BODY",BODY,{"disambiguationData":[OSD([sQuery(id+"F3.wireOp",EDGE,"E9")])]}),"instanceName":"128"});
            var Q129;
            Q129=makeQuery(id+"F5.opPattern","COPY",BODY,{"derivedFrom":makeQuery(id+"F4.opExtrude","SWEPT_BODY",BODY,{"disambiguationData":[OSD([sQuery(id+"F3.wireOp",EDGE,"E9")])]}),"instanceName":"129"});
            var Q130;
            Q130=makeQuery(id+"F5.opPattern","COPY",BODY,{"derivedFrom":makeQuery(id+"F4.opExtrude","SWEPT_BODY",BODY,{"disambiguationData":[OSD([sQuery(id+"F3.wireOp",EDGE,"E9")])]}),"instanceName":"130"});
            var Q131;
            Q131=makeQuery(id+"F5.opPattern","COPY",BODY,{"derivedFrom":makeQuery(id+"F4.opExtrude","SWEPT_BODY",BODY,{"disambiguationData":[OSD([sQuery(id+"F3.wireOp",EDGE,"E9")])]}),"instanceName":"131"});
            var Q132;
            Q132=makeQuery(id+"F5.opPattern","COPY",BODY,{"derivedFrom":makeQuery(id+"F4.opExtrude","SWEPT_BODY",BODY,{"disambiguationData":[OSD([sQuery(id+"F3.wireOp",EDGE,"E9")])]}),"instanceName":"132"});
            var Q133;
            Q133=makeQuery(id+"F5.opPattern","COPY",BODY,{"derivedFrom":makeQuery(id+"F4.opExtrude","SWEPT_BODY",BODY,{"disambiguationData":[OSD([sQuery(id+"F3.wireOp",EDGE,"E9")])]}),"instanceName":"133"});
            var Q134;
            Q134=makeQuery(id+"F5.opPattern","COPY",BODY,{"derivedFrom":makeQuery(id+"F4.opExtrude","SWEPT_BODY",BODY,{"disambiguationData":[OSD([sQuery(id+"F3.wireOp",EDGE,"E9")])]}),"instanceName":"134"});
            var Q135;
            Q135=makeQuery(id+"F5.opPattern","COPY",BODY,{"derivedFrom":makeQuery(id+"F4.opExtrude","SWEPT_BODY",BODY,{"disambiguationData":[OSD([sQuery(id+"F3.wireOp",EDGE,"E9")])]}),"instanceName":"135"});
            var Q136;
            Q136=makeQuery(id+"F5.opPattern","COPY",BODY,{"derivedFrom":makeQuery(id+"F4.opExtrude","SWEPT_BODY",BODY,{"disambiguationData":[OSD([sQuery(id+"F3.wireOp",EDGE,"E9")])]}),"instanceName":"136"});
            var Q137;
            Q137=makeQuery(id+"F5.opPattern","COPY",BODY,{"derivedFrom":makeQuery(id+"F4.opExtrude","SWEPT_BODY",BODY,{"disambiguationData":[OSD([sQuery(id+"F3.wireOp",EDGE,"E9")])]}),"instanceName":"137"});
            var Q138;
            Q138=makeQuery(id+"F5.opPattern","COPY",BODY,{"derivedFrom":makeQuery(id+"F4.opExtrude","SWEPT_BODY",BODY,{"disambiguationData":[OSD([sQuery(id+"F3.wireOp",EDGE,"E9")])]}),"instanceName":"138"});
            var Q139;
            Q139=makeQuery(id+"F5.opPattern","COPY",BODY,{"derivedFrom":makeQuery(id+"F4.opExtrude","SWEPT_BODY",BODY,{"disambiguationData":[OSD([sQuery(id+"F3.wireOp",EDGE,"E9")])]}),"instanceName":"139"});
            var Q140;
            Q140=makeQuery(id+"F5.opPattern","COPY",BODY,{"derivedFrom":makeQuery(id+"F4.opExtrude","SWEPT_BODY",BODY,{"disambiguationData":[OSD([sQuery(id+"F3.wireOp",EDGE,"E9")])]}),"instanceName":"140"});
            var Q141;
            Q141=makeQuery(id+"F5.opPattern","COPY",BODY,{"derivedFrom":makeQuery(id+"F4.opExtrude","SWEPT_BODY",BODY,{"disambiguationData":[OSD([sQuery(id+"F3.wireOp",EDGE,"E9")])]}),"instanceName":"141"});
            var Q142;
            Q142=makeQuery(id+"F5.opPattern","COPY",BODY,{"derivedFrom":makeQuery(id+"F4.opExtrude","SWEPT_BODY",BODY,{"disambiguationData":[OSD([sQuery(id+"F3.wireOp",EDGE,"E9")])]}),"instanceName":"142"});
            var Q143;
            Q143=makeQuery(id+"F5.opPattern","COPY",BODY,{"derivedFrom":makeQuery(id+"F4.opExtrude","SWEPT_BODY",BODY,{"disambiguationData":[OSD([sQuery(id+"F3.wireOp",EDGE,"E9")])]}),"instanceName":"143"});
            var Q144;
            Q144=makeQuery(id+"F5.opPattern","COPY",BODY,{"derivedFrom":makeQuery(id+"F4.opExtrude","SWEPT_BODY",BODY,{"disambiguationData":[OSD([sQuery(id+"F3.wireOp",EDGE,"E9")])]}),"instanceName":"144"});
            var Q145;
            Q145=makeQuery(id+"F5.opPattern","COPY",BODY,{"derivedFrom":makeQuery(id+"F4.opExtrude","SWEPT_BODY",BODY,{"disambiguationData":[OSD([sQuery(id+"F3.wireOp",EDGE,"E9")])]}),"instanceName":"145"});
            var Q146;
            Q146=makeQuery(id+"F5.opPattern","COPY",BODY,{"derivedFrom":makeQuery(id+"F4.opExtrude","SWEPT_BODY",BODY,{"disambiguationData":[OSD([sQuery(id+"F3.wireOp",EDGE,"E9")])]}),"instanceName":"146"});
            var Q147;
            Q147=makeQuery(id+"F5.opPattern","COPY",BODY,{"derivedFrom":makeQuery(id+"F4.opExtrude","SWEPT_BODY",BODY,{"disambiguationData":[OSD([sQuery(id+"F3.wireOp",EDGE,"E9")])]}),"instanceName":"147"});
            var Q148;
            Q148=makeQuery(id+"F5.opPattern","COPY",BODY,{"derivedFrom":makeQuery(id+"F4.opExtrude","SWEPT_BODY",BODY,{"disambiguationData":[OSD([sQuery(id+"F3.wireOp",EDGE,"E9")])]}),"instanceName":"148"});
            var Q149;
            Q149=makeQuery(id+"F5.opPattern","COPY",BODY,{"derivedFrom":makeQuery(id+"F4.opExtrude","SWEPT_BODY",BODY,{"disambiguationData":[OSD([sQuery(id+"F3.wireOp",EDGE,"E9")])]}),"instanceName":"149"});
            var Q150;
            Q150=makeQuery(id+"F5.opPattern","COPY",BODY,{"derivedFrom":makeQuery(id+"F4.opExtrude","SWEPT_BODY",BODY,{"disambiguationData":[OSD([sQuery(id+"F3.wireOp",EDGE,"E9")])]}),"instanceName":"150"});
            var Q151;
            Q151=makeQuery(id+"F5.opPattern","COPY",BODY,{"derivedFrom":makeQuery(id+"F4.opExtrude","SWEPT_BODY",BODY,{"disambiguationData":[OSD([sQuery(id+"F3.wireOp",EDGE,"E9")])]}),"instanceName":"151"});
            var Q152;
            Q152=makeQuery(id+"F5.opPattern","COPY",BODY,{"derivedFrom":makeQuery(id+"F4.opExtrude","SWEPT_BODY",BODY,{"disambiguationData":[OSD([sQuery(id+"F3.wireOp",EDGE,"E9")])]}),"instanceName":"152"});
            var Q153;
            Q153=makeQuery(id+"F5.opPattern","COPY",BODY,{"derivedFrom":makeQuery(id+"F4.opExtrude","SWEPT_BODY",BODY,{"disambiguationData":[OSD([sQuery(id+"F3.wireOp",EDGE,"E9")])]}),"instanceName":"153"});
            var Q154;
            Q154=makeQuery(id+"F5.opPattern","COPY",BODY,{"derivedFrom":makeQuery(id+"F4.opExtrude","SWEPT_BODY",BODY,{"disambiguationData":[OSD([sQuery(id+"F3.wireOp",EDGE,"E9")])]}),"instanceName":"154"});
            var Q155;
            Q155=makeQuery(id+"F5.opPattern","COPY",BODY,{"derivedFrom":makeQuery(id+"F4.opExtrude","SWEPT_BODY",BODY,{"disambiguationData":[OSD([sQuery(id+"F3.wireOp",EDGE,"E9")])]}),"instanceName":"155"});
            var Q156;
            Q156=makeQuery(id+"F5.opPattern","COPY",BODY,{"derivedFrom":makeQuery(id+"F4.opExtrude","SWEPT_BODY",BODY,{"disambiguationData":[OSD([sQuery(id+"F3.wireOp",EDGE,"E9")])]}),"instanceName":"156"});
            var Q157;
            Q157=makeQuery(id+"F5.opPattern","COPY",BODY,{"derivedFrom":makeQuery(id+"F4.opExtrude","SWEPT_BODY",BODY,{"disambiguationData":[OSD([sQuery(id+"F3.wireOp",EDGE,"E9")])]}),"instanceName":"157"});
            var Q158;
            Q158=makeQuery(id+"F5.opPattern","COPY",BODY,{"derivedFrom":makeQuery(id+"F4.opExtrude","SWEPT_BODY",BODY,{"disambiguationData":[OSD([sQuery(id+"F3.wireOp",EDGE,"E9")])]}),"instanceName":"158"});
            var Q159;
            Q159=makeQuery(id+"F5.opPattern","COPY",BODY,{"derivedFrom":makeQuery(id+"F4.opExtrude","SWEPT_BODY",BODY,{"disambiguationData":[OSD([sQuery(id+"F3.wireOp",EDGE,"E9")])]}),"instanceName":"159"});
            var Q160;
            Q160=makeQuery(id+"F5.opPattern","COPY",BODY,{"derivedFrom":makeQuery(id+"F4.opExtrude","SWEPT_BODY",BODY,{"disambiguationData":[OSD([sQuery(id+"F3.wireOp",EDGE,"E9")])]}),"instanceName":"160"});
            var Q161;
            Q161=makeQuery(id+"F5.opPattern","COPY",BODY,{"derivedFrom":makeQuery(id+"F4.opExtrude","SWEPT_BODY",BODY,{"disambiguationData":[OSD([sQuery(id+"F3.wireOp",EDGE,"E9")])]}),"instanceName":"161"});
            var Q162;
            Q162=makeQuery(id+"F5.opPattern","COPY",BODY,{"derivedFrom":makeQuery(id+"F4.opExtrude","SWEPT_BODY",BODY,{"disambiguationData":[OSD([sQuery(id+"F3.wireOp",EDGE,"E9")])]}),"instanceName":"162"});
            var Q163;
            Q163=makeQuery(id+"F5.opPattern","COPY",BODY,{"derivedFrom":makeQuery(id+"F4.opExtrude","SWEPT_BODY",BODY,{"disambiguationData":[OSD([sQuery(id+"F3.wireOp",EDGE,"E9")])]}),"instanceName":"163"});
            var Q164;
            Q164=makeQuery(id+"F5.opPattern","COPY",BODY,{"derivedFrom":makeQuery(id+"F4.opExtrude","SWEPT_BODY",BODY,{"disambiguationData":[OSD([sQuery(id+"F3.wireOp",EDGE,"E9")])]}),"instanceName":"164"});
            var Q165;
            Q165=makeQuery(id+"F5.opPattern","COPY",BODY,{"derivedFrom":makeQuery(id+"F4.opExtrude","SWEPT_BODY",BODY,{"disambiguationData":[OSD([sQuery(id+"F3.wireOp",EDGE,"E9")])]}),"instanceName":"165"});
            var Q166;
            Q166=makeQuery(id+"F5.opPattern","COPY",BODY,{"derivedFrom":makeQuery(id+"F4.opExtrude","SWEPT_BODY",BODY,{"disambiguationData":[OSD([sQuery(id+"F3.wireOp",EDGE,"E9")])]}),"instanceName":"166"});
            var Q167;
            Q167=makeQuery(id+"F5.opPattern","COPY",BODY,{"derivedFrom":makeQuery(id+"F4.opExtrude","SWEPT_BODY",BODY,{"disambiguationData":[OSD([sQuery(id+"F3.wireOp",EDGE,"E9")])]}),"instanceName":"167"});
            var Q168;
            Q168=makeQuery(id+"F5.opPattern","COPY",BODY,{"derivedFrom":makeQuery(id+"F4.opExtrude","SWEPT_BODY",BODY,{"disambiguationData":[OSD([sQuery(id+"F3.wireOp",EDGE,"E9")])]}),"instanceName":"168"});
            var Q169;
            Q169=makeQuery(id+"F5.opPattern","COPY",BODY,{"derivedFrom":makeQuery(id+"F4.opExtrude","SWEPT_BODY",BODY,{"disambiguationData":[OSD([sQuery(id+"F3.wireOp",EDGE,"E9")])]}),"instanceName":"169"});
            var Q170;
            Q170=makeQuery(id+"F5.opPattern","COPY",BODY,{"derivedFrom":makeQuery(id+"F4.opExtrude","SWEPT_BODY",BODY,{"disambiguationData":[OSD([sQuery(id+"F3.wireOp",EDGE,"E9")])]}),"instanceName":"170"});
            var Q171;
            Q171=makeQuery(id+"F5.opPattern","COPY",BODY,{"derivedFrom":makeQuery(id+"F4.opExtrude","SWEPT_BODY",BODY,{"disambiguationData":[OSD([sQuery(id+"F3.wireOp",EDGE,"E9")])]}),"instanceName":"171"});
            var Q172;
            Q172=makeQuery(id+"F5.opPattern","COPY",BODY,{"derivedFrom":makeQuery(id+"F4.opExtrude","SWEPT_BODY",BODY,{"disambiguationData":[OSD([sQuery(id+"F3.wireOp",EDGE,"E9")])]}),"instanceName":"172"});
            var Q173;
            Q173=makeQuery(id+"F5.opPattern","COPY",BODY,{"derivedFrom":makeQuery(id+"F4.opExtrude","SWEPT_BODY",BODY,{"disambiguationData":[OSD([sQuery(id+"F3.wireOp",EDGE,"E9")])]}),"instanceName":"173"});
            var Q174;
            Q174=makeQuery(id+"F5.opPattern","COPY",BODY,{"derivedFrom":makeQuery(id+"F4.opExtrude","SWEPT_BODY",BODY,{"disambiguationData":[OSD([sQuery(id+"F3.wireOp",EDGE,"E9")])]}),"instanceName":"174"});
            var Q175;
            Q175=makeQuery(id+"F5.opPattern","COPY",BODY,{"derivedFrom":makeQuery(id+"F4.opExtrude","SWEPT_BODY",BODY,{"disambiguationData":[OSD([sQuery(id+"F3.wireOp",EDGE,"E9")])]}),"instanceName":"175"});
            var Q176;
            Q176=makeQuery(id+"F5.opPattern","COPY",BODY,{"derivedFrom":makeQuery(id+"F4.opExtrude","SWEPT_BODY",BODY,{"disambiguationData":[OSD([sQuery(id+"F3.wireOp",EDGE,"E9")])]}),"instanceName":"176"});
            var Q177;
            Q177=makeQuery(id+"F5.opPattern","COPY",BODY,{"derivedFrom":makeQuery(id+"F4.opExtrude","SWEPT_BODY",BODY,{"disambiguationData":[OSD([sQuery(id+"F3.wireOp",EDGE,"E9")])]}),"instanceName":"177"});
            var Q178;
            Q178=makeQuery(id+"F5.opPattern","COPY",BODY,{"derivedFrom":makeQuery(id+"F4.opExtrude","SWEPT_BODY",BODY,{"disambiguationData":[OSD([sQuery(id+"F3.wireOp",EDGE,"E9")])]}),"instanceName":"178"});
            var Q179;
            Q179=makeQuery(id+"F5.opPattern","COPY",BODY,{"derivedFrom":makeQuery(id+"F4.opExtrude","SWEPT_BODY",BODY,{"disambiguationData":[OSD([sQuery(id+"F3.wireOp",EDGE,"E9")])]}),"instanceName":"179"});
            var Q180;
            Q180=makeQuery(id+"F5.opPattern","COPY",BODY,{"derivedFrom":makeQuery(id+"F4.opExtrude","SWEPT_BODY",BODY,{"disambiguationData":[OSD([sQuery(id+"F3.wireOp",EDGE,"E9")])]}),"instanceName":"180"});
            var Q181;
            Q181=makeQuery(id+"F5.opPattern","COPY",BODY,{"derivedFrom":makeQuery(id+"F4.opExtrude","SWEPT_BODY",BODY,{"disambiguationData":[OSD([sQuery(id+"F3.wireOp",EDGE,"E9")])]}),"instanceName":"181"});
            var Q182;
            Q182=makeQuery(id+"F5.opPattern","COPY",BODY,{"derivedFrom":makeQuery(id+"F4.opExtrude","SWEPT_BODY",BODY,{"disambiguationData":[OSD([sQuery(id+"F3.wireOp",EDGE,"E9")])]}),"instanceName":"182"});
            var Q183;
            Q183=makeQuery(id+"F5.opPattern","COPY",BODY,{"derivedFrom":makeQuery(id+"F4.opExtrude","SWEPT_BODY",BODY,{"disambiguationData":[OSD([sQuery(id+"F3.wireOp",EDGE,"E9")])]}),"instanceName":"183"});
            var Q184;
            Q184=makeQuery(id+"F5.opPattern","COPY",BODY,{"derivedFrom":makeQuery(id+"F4.opExtrude","SWEPT_BODY",BODY,{"disambiguationData":[OSD([sQuery(id+"F3.wireOp",EDGE,"E9")])]}),"instanceName":"184"});
            var Q185;
            Q185=makeQuery(id+"F5.opPattern","COPY",BODY,{"derivedFrom":makeQuery(id+"F4.opExtrude","SWEPT_BODY",BODY,{"disambiguationData":[OSD([sQuery(id+"F3.wireOp",EDGE,"E9")])]}),"instanceName":"185"});
            var Q186;
            Q186=makeQuery(id+"F5.opPattern","COPY",BODY,{"derivedFrom":makeQuery(id+"F4.opExtrude","SWEPT_BODY",BODY,{"disambiguationData":[OSD([sQuery(id+"F3.wireOp",EDGE,"E9")])]}),"instanceName":"186"});
            var Q187;
            Q187=makeQuery(id+"F5.opPattern","COPY",BODY,{"derivedFrom":makeQuery(id+"F4.opExtrude","SWEPT_BODY",BODY,{"disambiguationData":[OSD([sQuery(id+"F3.wireOp",EDGE,"E9")])]}),"instanceName":"187"});
            var Q188;
            Q188=makeQuery(id+"F5.opPattern","COPY",BODY,{"derivedFrom":makeQuery(id+"F4.opExtrude","SWEPT_BODY",BODY,{"disambiguationData":[OSD([sQuery(id+"F3.wireOp",EDGE,"E9")])]}),"instanceName":"188"});
            var Q189;
            Q189=makeQuery(id+"F5.opPattern","COPY",BODY,{"derivedFrom":makeQuery(id+"F4.opExtrude","SWEPT_BODY",BODY,{"disambiguationData":[OSD([sQuery(id+"F3.wireOp",EDGE,"E9")])]}),"instanceName":"189"});
            var Q190;
            Q190=makeQuery(id+"F5.opPattern","COPY",BODY,{"derivedFrom":makeQuery(id+"F4.opExtrude","SWEPT_BODY",BODY,{"disambiguationData":[OSD([sQuery(id+"F3.wireOp",EDGE,"E9")])]}),"instanceName":"190"});
            var Q191;
            Q191=makeQuery(id+"F5.opPattern","COPY",BODY,{"derivedFrom":makeQuery(id+"F4.opExtrude","SWEPT_BODY",BODY,{"disambiguationData":[OSD([sQuery(id+"F3.wireOp",EDGE,"E9")])]}),"instanceName":"191"});
            var Q192;
            Q192=makeQuery(id+"F5.opPattern","COPY",BODY,{"derivedFrom":makeQuery(id+"F4.opExtrude","SWEPT_BODY",BODY,{"disambiguationData":[OSD([sQuery(id+"F3.wireOp",EDGE,"E9")])]}),"instanceName":"192"});
            var Q193;
            Q193=makeQuery(id+"F5.opPattern","COPY",BODY,{"derivedFrom":makeQuery(id+"F4.opExtrude","SWEPT_BODY",BODY,{"disambiguationData":[OSD([sQuery(id+"F3.wireOp",EDGE,"E9")])]}),"instanceName":"193"});
            var Q194;
            Q194=makeQuery(id+"F5.opPattern","COPY",BODY,{"derivedFrom":makeQuery(id+"F4.opExtrude","SWEPT_BODY",BODY,{"disambiguationData":[OSD([sQuery(id+"F3.wireOp",EDGE,"E9")])]}),"instanceName":"194"});
            var Q195;
            Q195=makeQuery(id+"F5.opPattern","COPY",BODY,{"derivedFrom":makeQuery(id+"F4.opExtrude","SWEPT_BODY",BODY,{"disambiguationData":[OSD([sQuery(id+"F3.wireOp",EDGE,"E9")])]}),"instanceName":"195"});
            var Q196;
            Q196=makeQuery(id+"F5.opPattern","COPY",BODY,{"derivedFrom":makeQuery(id+"F4.opExtrude","SWEPT_BODY",BODY,{"disambiguationData":[OSD([sQuery(id+"F3.wireOp",EDGE,"E9")])]}),"instanceName":"196"});
            var Q197;
            Q197=makeQuery(id+"F5.opPattern","COPY",BODY,{"derivedFrom":makeQuery(id+"F4.opExtrude","SWEPT_BODY",BODY,{"disambiguationData":[OSD([sQuery(id+"F3.wireOp",EDGE,"E9")])]}),"instanceName":"197"});
            var Q198;
            Q198=makeQuery(id+"F5.opPattern","COPY",BODY,{"derivedFrom":makeQuery(id+"F4.opExtrude","SWEPT_BODY",BODY,{"disambiguationData":[OSD([sQuery(id+"F3.wireOp",EDGE,"E9")])]}),"instanceName":"198"});
            var Q199;
            Q199=makeQuery(id+"F5.opPattern","COPY",BODY,{"derivedFrom":makeQuery(id+"F4.opExtrude","SWEPT_BODY",BODY,{"disambiguationData":[OSD([sQuery(id+"F3.wireOp",EDGE,"E9")])]}),"instanceName":"199"});
            var Q200;
            Q200=makeQuery(id+"F5.opPattern","COPY",BODY,{"derivedFrom":makeQuery(id+"F4.opExtrude","SWEPT_BODY",BODY,{"disambiguationData":[OSD([sQuery(id+"F3.wireOp",EDGE,"E9")])]}),"instanceName":"200"});
            var Q201;
            Q201=makeQuery(id+"F5.opPattern","COPY",BODY,{"derivedFrom":makeQuery(id+"F4.opExtrude","SWEPT_BODY",BODY,{"disambiguationData":[OSD([sQuery(id+"F3.wireOp",EDGE,"E9")])]}),"instanceName":"201"});
            var Q202;
            Q202=makeQuery(id+"F5.opPattern","COPY",BODY,{"derivedFrom":makeQuery(id+"F4.opExtrude","SWEPT_BODY",BODY,{"disambiguationData":[OSD([sQuery(id+"F3.wireOp",EDGE,"E9")])]}),"instanceName":"202"});
            var Q203;
            Q203=makeQuery(id+"F5.opPattern","COPY",BODY,{"derivedFrom":makeQuery(id+"F4.opExtrude","SWEPT_BODY",BODY,{"disambiguationData":[OSD([sQuery(id+"F3.wireOp",EDGE,"E9")])]}),"instanceName":"203"});
            var Q204;
            Q204=makeQuery(id+"F5.opPattern","COPY",BODY,{"derivedFrom":makeQuery(id+"F4.opExtrude","SWEPT_BODY",BODY,{"disambiguationData":[OSD([sQuery(id+"F3.wireOp",EDGE,"E9")])]}),"instanceName":"204"});
            var Q205;
            Q205=makeQuery(id+"F5.opPattern","COPY",BODY,{"derivedFrom":makeQuery(id+"F4.opExtrude","SWEPT_BODY",BODY,{"disambiguationData":[OSD([sQuery(id+"F3.wireOp",EDGE,"E9")])]}),"instanceName":"205"});
            var Q206;
            Q206=makeQuery(id+"F5.opPattern","COPY",BODY,{"derivedFrom":makeQuery(id+"F4.opExtrude","SWEPT_BODY",BODY,{"disambiguationData":[OSD([sQuery(id+"F3.wireOp",EDGE,"E9")])]}),"instanceName":"206"});
            var Q207;
            Q207=makeQuery(id+"F5.opPattern","COPY",BODY,{"derivedFrom":makeQuery(id+"F4.opExtrude","SWEPT_BODY",BODY,{"disambiguationData":[OSD([sQuery(id+"F3.wireOp",EDGE,"E9")])]}),"instanceName":"207"});
            var Q208;
            Q208=makeQuery(id+"F5.opPattern","COPY",BODY,{"derivedFrom":makeQuery(id+"F4.opExtrude","SWEPT_BODY",BODY,{"disambiguationData":[OSD([sQuery(id+"F3.wireOp",EDGE,"E9")])]}),"instanceName":"208"});
            var Q209;
            Q209=makeQuery(id+"F5.opPattern","COPY",BODY,{"derivedFrom":makeQuery(id+"F4.opExtrude","SWEPT_BODY",BODY,{"disambiguationData":[OSD([sQuery(id+"F3.wireOp",EDGE,"E9")])]}),"instanceName":"209"});
            var Q210;
            Q210=makeQuery(id+"F5.opPattern","COPY",BODY,{"derivedFrom":makeQuery(id+"F4.opExtrude","SWEPT_BODY",BODY,{"disambiguationData":[OSD([sQuery(id+"F3.wireOp",EDGE,"E9")])]}),"instanceName":"210"});
            var Q211;
            Q211=makeQuery(id+"F5.opPattern","COPY",BODY,{"derivedFrom":makeQuery(id+"F4.opExtrude","SWEPT_BODY",BODY,{"disambiguationData":[OSD([sQuery(id+"F3.wireOp",EDGE,"E9")])]}),"instanceName":"211"});
            var Q212;
            Q212=makeQuery(id+"F5.opPattern","COPY",BODY,{"derivedFrom":makeQuery(id+"F4.opExtrude","SWEPT_BODY",BODY,{"disambiguationData":[OSD([sQuery(id+"F3.wireOp",EDGE,"E9")])]}),"instanceName":"212"});
            var Q213;
            Q213=makeQuery(id+"F5.opPattern","COPY",BODY,{"derivedFrom":makeQuery(id+"F4.opExtrude","SWEPT_BODY",BODY,{"disambiguationData":[OSD([sQuery(id+"F3.wireOp",EDGE,"E9")])]}),"instanceName":"213"});
            var Q214;
            Q214=makeQuery(id+"F5.opPattern","COPY",BODY,{"derivedFrom":makeQuery(id+"F4.opExtrude","SWEPT_BODY",BODY,{"disambiguationData":[OSD([sQuery(id+"F3.wireOp",EDGE,"E9")])]}),"instanceName":"214"});
            var Q215;
            Q215=makeQuery(id+"F5.opPattern","COPY",BODY,{"derivedFrom":makeQuery(id+"F4.opExtrude","SWEPT_BODY",BODY,{"disambiguationData":[OSD([sQuery(id+"F3.wireOp",EDGE,"E9")])]}),"instanceName":"215"});
            var Q216;
            Q216=makeQuery(id+"F5.opPattern","COPY",BODY,{"derivedFrom":makeQuery(id+"F4.opExtrude","SWEPT_BODY",BODY,{"disambiguationData":[OSD([sQuery(id+"F3.wireOp",EDGE,"E9")])]}),"instanceName":"216"});
            var Q217;
            Q217=makeQuery(id+"F5.opPattern","COPY",BODY,{"derivedFrom":makeQuery(id+"F4.opExtrude","SWEPT_BODY",BODY,{"disambiguationData":[OSD([sQuery(id+"F3.wireOp",EDGE,"E9")])]}),"instanceName":"217"});
            var Q218;
            Q218=makeQuery(id+"F5.opPattern","COPY",BODY,{"derivedFrom":makeQuery(id+"F4.opExtrude","SWEPT_BODY",BODY,{"disambiguationData":[OSD([sQuery(id+"F3.wireOp",EDGE,"E9")])]}),"instanceName":"218"});
            var Q219;
            Q219=makeQuery(id+"F5.opPattern","COPY",BODY,{"derivedFrom":makeQuery(id+"F4.opExtrude","SWEPT_BODY",BODY,{"disambiguationData":[OSD([sQuery(id+"F3.wireOp",EDGE,"E9")])]}),"instanceName":"219"});
            var Q220;
            Q220=makeQuery(id+"F5.opPattern","COPY",BODY,{"derivedFrom":makeQuery(id+"F4.opExtrude","SWEPT_BODY",BODY,{"disambiguationData":[OSD([sQuery(id+"F3.wireOp",EDGE,"E9")])]}),"instanceName":"220"});
            var Q221;
            Q221=makeQuery(id+"F5.opPattern","COPY",BODY,{"derivedFrom":makeQuery(id+"F4.opExtrude","SWEPT_BODY",BODY,{"disambiguationData":[OSD([sQuery(id+"F3.wireOp",EDGE,"E9")])]}),"instanceName":"221"});
            var Q222;
            Q222=makeQuery(id+"F5.opPattern","COPY",BODY,{"derivedFrom":makeQuery(id+"F4.opExtrude","SWEPT_BODY",BODY,{"disambiguationData":[OSD([sQuery(id+"F3.wireOp",EDGE,"E9")])]}),"instanceName":"222"});
            var Q223;
            Q223=makeQuery(id+"F5.opPattern","COPY",BODY,{"derivedFrom":makeQuery(id+"F4.opExtrude","SWEPT_BODY",BODY,{"disambiguationData":[OSD([sQuery(id+"F3.wireOp",EDGE,"E9")])]}),"instanceName":"223"});
            var Q224;
            Q224=makeQuery(id+"F5.opPattern","COPY",BODY,{"derivedFrom":makeQuery(id+"F4.opExtrude","SWEPT_BODY",BODY,{"disambiguationData":[OSD([sQuery(id+"F3.wireOp",EDGE,"E9")])]}),"instanceName":"224"});
            var Q225;
            Q225=makeQuery(id+"F5.opPattern","COPY",BODY,{"derivedFrom":makeQuery(id+"F4.opExtrude","SWEPT_BODY",BODY,{"disambiguationData":[OSD([sQuery(id+"F3.wireOp",EDGE,"E9")])]}),"instanceName":"225"});
            var Q226;
            Q226=makeQuery(id+"F5.opPattern","COPY",BODY,{"derivedFrom":makeQuery(id+"F4.opExtrude","SWEPT_BODY",BODY,{"disambiguationData":[OSD([sQuery(id+"F3.wireOp",EDGE,"E9")])]}),"instanceName":"226"});
            var Q227;
            Q227=makeQuery(id+"F5.opPattern","COPY",BODY,{"derivedFrom":makeQuery(id+"F4.opExtrude","SWEPT_BODY",BODY,{"disambiguationData":[OSD([sQuery(id+"F3.wireOp",EDGE,"E9")])]}),"instanceName":"227"});
            var Q228;
            Q228=makeQuery(id+"F5.opPattern","COPY",BODY,{"derivedFrom":makeQuery(id+"F4.opExtrude","SWEPT_BODY",BODY,{"disambiguationData":[OSD([sQuery(id+"F3.wireOp",EDGE,"E9")])]}),"instanceName":"228"});
            var Q229;
            Q229=makeQuery(id+"F5.opPattern","COPY",BODY,{"derivedFrom":makeQuery(id+"F4.opExtrude","SWEPT_BODY",BODY,{"disambiguationData":[OSD([sQuery(id+"F3.wireOp",EDGE,"E9")])]}),"instanceName":"229"});
            var Q230;
            Q230=makeQuery(id+"F5.opPattern","COPY",BODY,{"derivedFrom":makeQuery(id+"F4.opExtrude","SWEPT_BODY",BODY,{"disambiguationData":[OSD([sQuery(id+"F3.wireOp",EDGE,"E9")])]}),"instanceName":"230"});
            var Q231;
            Q231=makeQuery(id+"F5.opPattern","COPY",BODY,{"derivedFrom":makeQuery(id+"F4.opExtrude","SWEPT_BODY",BODY,{"disambiguationData":[OSD([sQuery(id+"F3.wireOp",EDGE,"E9")])]}),"instanceName":"231"});
            var Q232;
            Q232=makeQuery(id+"F5.opPattern","COPY",BODY,{"derivedFrom":makeQuery(id+"F4.opExtrude","SWEPT_BODY",BODY,{"disambiguationData":[OSD([sQuery(id+"F3.wireOp",EDGE,"E9")])]}),"instanceName":"232"});
            var Q233;
            Q233=makeQuery(id+"F5.opPattern","COPY",BODY,{"derivedFrom":makeQuery(id+"F4.opExtrude","SWEPT_BODY",BODY,{"disambiguationData":[OSD([sQuery(id+"F3.wireOp",EDGE,"E9")])]}),"instanceName":"233"});
            var Q234;
            Q234=makeQuery(id+"F5.opPattern","COPY",BODY,{"derivedFrom":makeQuery(id+"F4.opExtrude","SWEPT_BODY",BODY,{"disambiguationData":[OSD([sQuery(id+"F3.wireOp",EDGE,"E9")])]}),"instanceName":"234"});
            var Q235;
            Q235=makeQuery(id+"F5.opPattern","COPY",BODY,{"derivedFrom":makeQuery(id+"F4.opExtrude","SWEPT_BODY",BODY,{"disambiguationData":[OSD([sQuery(id+"F3.wireOp",EDGE,"E9")])]}),"instanceName":"235"});
            var Q236;
            Q236=makeQuery(id+"F5.opPattern","COPY",BODY,{"derivedFrom":makeQuery(id+"F4.opExtrude","SWEPT_BODY",BODY,{"disambiguationData":[OSD([sQuery(id+"F3.wireOp",EDGE,"E9")])]}),"instanceName":"236"});
            var Q237;
            Q237=makeQuery(id+"F5.opPattern","COPY",BODY,{"derivedFrom":makeQuery(id+"F4.opExtrude","SWEPT_BODY",BODY,{"disambiguationData":[OSD([sQuery(id+"F3.wireOp",EDGE,"E9")])]}),"instanceName":"237"});
            var Q238;
            Q238=makeQuery(id+"F5.opPattern","COPY",BODY,{"derivedFrom":makeQuery(id+"F4.opExtrude","SWEPT_BODY",BODY,{"disambiguationData":[OSD([sQuery(id+"F3.wireOp",EDGE,"E9")])]}),"instanceName":"238"});
            var Q239;
            Q239=makeQuery(id+"F5.opPattern","COPY",BODY,{"derivedFrom":makeQuery(id+"F4.opExtrude","SWEPT_BODY",BODY,{"disambiguationData":[OSD([sQuery(id+"F3.wireOp",EDGE,"E9")])]}),"instanceName":"239"});
            var Q240;
            Q240=makeQuery(id+"F5.opPattern","COPY",BODY,{"derivedFrom":makeQuery(id+"F4.opExtrude","SWEPT_BODY",BODY,{"disambiguationData":[OSD([sQuery(id+"F3.wireOp",EDGE,"E9")])]}),"instanceName":"240"});
            var Q241;
            Q241=makeQuery(id+"F5.opPattern","COPY",BODY,{"derivedFrom":makeQuery(id+"F4.opExtrude","SWEPT_BODY",BODY,{"disambiguationData":[OSD([sQuery(id+"F3.wireOp",EDGE,"E9")])]}),"instanceName":"241"});
            var Q242;
            Q242=makeQuery(id+"F5.opPattern","COPY",BODY,{"derivedFrom":makeQuery(id+"F4.opExtrude","SWEPT_BODY",BODY,{"disambiguationData":[OSD([sQuery(id+"F3.wireOp",EDGE,"E9")])]}),"instanceName":"242"});
            var Q243;
            Q243=makeQuery(id+"F5.opPattern","COPY",BODY,{"derivedFrom":makeQuery(id+"F4.opExtrude","SWEPT_BODY",BODY,{"disambiguationData":[OSD([sQuery(id+"F3.wireOp",EDGE,"E9")])]}),"instanceName":"243"});
            var Q244;
            Q244=makeQuery(id+"F5.opPattern","COPY",BODY,{"derivedFrom":makeQuery(id+"F4.opExtrude","SWEPT_BODY",BODY,{"disambiguationData":[OSD([sQuery(id+"F3.wireOp",EDGE,"E9")])]}),"instanceName":"244"});
            var Q245;
            Q245=makeQuery(id+"F5.opPattern","COPY",BODY,{"derivedFrom":makeQuery(id+"F4.opExtrude","SWEPT_BODY",BODY,{"disambiguationData":[OSD([sQuery(id+"F3.wireOp",EDGE,"E9")])]}),"instanceName":"245"});
            var Q246;
            Q246=makeQuery(id+"F5.opPattern","COPY",BODY,{"derivedFrom":makeQuery(id+"F4.opExtrude","SWEPT_BODY",BODY,{"disambiguationData":[OSD([sQuery(id+"F3.wireOp",EDGE,"E9")])]}),"instanceName":"246"});
            var Q247;
            Q247=makeQuery(id+"F5.opPattern","COPY",BODY,{"derivedFrom":makeQuery(id+"F4.opExtrude","SWEPT_BODY",BODY,{"disambiguationData":[OSD([sQuery(id+"F3.wireOp",EDGE,"E9")])]}),"instanceName":"247"});
            var Q248;
            Q248=makeQuery(id+"F5.opPattern","COPY",BODY,{"derivedFrom":makeQuery(id+"F4.opExtrude","SWEPT_BODY",BODY,{"disambiguationData":[OSD([sQuery(id+"F3.wireOp",EDGE,"E9")])]}),"instanceName":"248"});
            var Q249;
            Q249=makeQuery(id+"F5.opPattern","COPY",BODY,{"derivedFrom":makeQuery(id+"F4.opExtrude","SWEPT_BODY",BODY,{"disambiguationData":[OSD([sQuery(id+"F3.wireOp",EDGE,"E9")])]}),"instanceName":"249"});
            var Q250;
            Q250=makeQuery(id+"F5.opPattern","COPY",BODY,{"derivedFrom":makeQuery(id+"F4.opExtrude","SWEPT_BODY",BODY,{"disambiguationData":[OSD([sQuery(id+"F3.wireOp",EDGE,"E9")])]}),"instanceName":"250"});
            var Q251;
            Q251=makeQuery(id+"F5.opPattern","COPY",BODY,{"derivedFrom":makeQuery(id+"F4.opExtrude","SWEPT_BODY",BODY,{"disambiguationData":[OSD([sQuery(id+"F3.wireOp",EDGE,"E9")])]}),"instanceName":"251"});
            var Q252;
            Q252=makeQuery(id+"F5.opPattern","COPY",BODY,{"derivedFrom":makeQuery(id+"F4.opExtrude","SWEPT_BODY",BODY,{"disambiguationData":[OSD([sQuery(id+"F3.wireOp",EDGE,"E9")])]}),"instanceName":"252"});
            var Q253;
            Q253=makeQuery(id+"F5.opPattern","COPY",BODY,{"derivedFrom":makeQuery(id+"F4.opExtrude","SWEPT_BODY",BODY,{"disambiguationData":[OSD([sQuery(id+"F3.wireOp",EDGE,"E9")])]}),"instanceName":"253"});
            var Q254;
            Q254=makeQuery(id+"F5.opPattern","COPY",BODY,{"derivedFrom":makeQuery(id+"F4.opExtrude","SWEPT_BODY",BODY,{"disambiguationData":[OSD([sQuery(id+"F3.wireOp",EDGE,"E9")])]}),"instanceName":"254"});
            var Q255;
            Q255=makeQuery(id+"F5.opPattern","COPY",BODY,{"derivedFrom":makeQuery(id+"F4.opExtrude","SWEPT_BODY",BODY,{"disambiguationData":[OSD([sQuery(id+"F3.wireOp",EDGE,"E9")])]}),"instanceName":"255"});
            var Q256;
            Q256=makeQuery(id+"F5.opPattern","COPY",BODY,{"derivedFrom":makeQuery(id+"F4.opExtrude","SWEPT_BODY",BODY,{"disambiguationData":[OSD([sQuery(id+"F3.wireOp",EDGE,"E9")])]}),"instanceName":"256"});
            var Q257;
            Q257=makeQuery(id+"F5.opPattern","COPY",BODY,{"derivedFrom":makeQuery(id+"F4.opExtrude","SWEPT_BODY",BODY,{"disambiguationData":[OSD([sQuery(id+"F3.wireOp",EDGE,"E9")])]}),"instanceName":"257"});
            var Q258;
            Q258=makeQuery(id+"F5.opPattern","COPY",BODY,{"derivedFrom":makeQuery(id+"F4.opExtrude","SWEPT_BODY",BODY,{"disambiguationData":[OSD([sQuery(id+"F3.wireOp",EDGE,"E9")])]}),"instanceName":"258"});
            var Q259;
            Q259=makeQuery(id+"F5.opPattern","COPY",BODY,{"derivedFrom":makeQuery(id+"F4.opExtrude","SWEPT_BODY",BODY,{"disambiguationData":[OSD([sQuery(id+"F3.wireOp",EDGE,"E9")])]}),"instanceName":"259"});
            var Q260;
            Q260=makeQuery(id+"F5.opPattern","COPY",BODY,{"derivedFrom":makeQuery(id+"F4.opExtrude","SWEPT_BODY",BODY,{"disambiguationData":[OSD([sQuery(id+"F3.wireOp",EDGE,"E9")])]}),"instanceName":"260"});
            var Q261;
            Q261=makeQuery(id+"F5.opPattern","COPY",BODY,{"derivedFrom":makeQuery(id+"F4.opExtrude","SWEPT_BODY",BODY,{"disambiguationData":[OSD([sQuery(id+"F3.wireOp",EDGE,"E9")])]}),"instanceName":"261"});
            var Q262;
            Q262=makeQuery(id+"F5.opPattern","COPY",BODY,{"derivedFrom":makeQuery(id+"F4.opExtrude","SWEPT_BODY",BODY,{"disambiguationData":[OSD([sQuery(id+"F3.wireOp",EDGE,"E9")])]}),"instanceName":"262"});
            var Q263;
            Q263=makeQuery(id+"F5.opPattern","COPY",BODY,{"derivedFrom":makeQuery(id+"F4.opExtrude","SWEPT_BODY",BODY,{"disambiguationData":[OSD([sQuery(id+"F3.wireOp",EDGE,"E9")])]}),"instanceName":"263"});
            var Q264;
            Q264=makeQuery(id+"F5.opPattern","COPY",BODY,{"derivedFrom":makeQuery(id+"F4.opExtrude","SWEPT_BODY",BODY,{"disambiguationData":[OSD([sQuery(id+"F3.wireOp",EDGE,"E9")])]}),"instanceName":"264"});
            var Q265;
            Q265=makeQuery(id+"F5.opPattern","COPY",BODY,{"derivedFrom":makeQuery(id+"F4.opExtrude","SWEPT_BODY",BODY,{"disambiguationData":[OSD([sQuery(id+"F3.wireOp",EDGE,"E9")])]}),"instanceName":"265"});
            var Q266;
            Q266=makeQuery(id+"F5.opPattern","COPY",BODY,{"derivedFrom":makeQuery(id+"F4.opExtrude","SWEPT_BODY",BODY,{"disambiguationData":[OSD([sQuery(id+"F3.wireOp",EDGE,"E9")])]}),"instanceName":"266"});
            var Q267;
            Q267=makeQuery(id+"F5.opPattern","COPY",BODY,{"derivedFrom":makeQuery(id+"F4.opExtrude","SWEPT_BODY",BODY,{"disambiguationData":[OSD([sQuery(id+"F3.wireOp",EDGE,"E9")])]}),"instanceName":"267"});
            var Q268;
            Q268=makeQuery(id+"F5.opPattern","COPY",BODY,{"derivedFrom":makeQuery(id+"F4.opExtrude","SWEPT_BODY",BODY,{"disambiguationData":[OSD([sQuery(id+"F3.wireOp",EDGE,"E9")])]}),"instanceName":"268"});
            var Q269;
            Q269=makeQuery(id+"F5.opPattern","COPY",BODY,{"derivedFrom":makeQuery(id+"F4.opExtrude","SWEPT_BODY",BODY,{"disambiguationData":[OSD([sQuery(id+"F3.wireOp",EDGE,"E9")])]}),"instanceName":"269"});
            var Q270;
            Q270=makeQuery(id+"F5.opPattern","COPY",BODY,{"derivedFrom":makeQuery(id+"F4.opExtrude","SWEPT_BODY",BODY,{"disambiguationData":[OSD([sQuery(id+"F3.wireOp",EDGE,"E9")])]}),"instanceName":"270"});
            var Q271;
            Q271=makeQuery(id+"F5.opPattern","COPY",BODY,{"derivedFrom":makeQuery(id+"F4.opExtrude","SWEPT_BODY",BODY,{"disambiguationData":[OSD([sQuery(id+"F3.wireOp",EDGE,"E9")])]}),"instanceName":"271"});
            var Q272;
            Q272=makeQuery(id+"F5.opPattern","COPY",BODY,{"derivedFrom":makeQuery(id+"F4.opExtrude","SWEPT_BODY",BODY,{"disambiguationData":[OSD([sQuery(id+"F3.wireOp",EDGE,"E9")])]}),"instanceName":"272"});
            var Q273;
            Q273=makeQuery(id+"F5.opPattern","COPY",BODY,{"derivedFrom":makeQuery(id+"F4.opExtrude","SWEPT_BODY",BODY,{"disambiguationData":[OSD([sQuery(id+"F3.wireOp",EDGE,"E9")])]}),"instanceName":"273"});
            var Q274;
            Q274=makeQuery(id+"F5.opPattern","COPY",BODY,{"derivedFrom":makeQuery(id+"F4.opExtrude","SWEPT_BODY",BODY,{"disambiguationData":[OSD([sQuery(id+"F3.wireOp",EDGE,"E9")])]}),"instanceName":"274"});
            var Q275;
            Q275=makeQuery(id+"F5.opPattern","COPY",BODY,{"derivedFrom":makeQuery(id+"F4.opExtrude","SWEPT_BODY",BODY,{"disambiguationData":[OSD([sQuery(id+"F3.wireOp",EDGE,"E9")])]}),"instanceName":"275"});
            var Q276;
            Q276=makeQuery(id+"F5.opPattern","COPY",BODY,{"derivedFrom":makeQuery(id+"F4.opExtrude","SWEPT_BODY",BODY,{"disambiguationData":[OSD([sQuery(id+"F3.wireOp",EDGE,"E9")])]}),"instanceName":"276"});
            var Q277;
            Q277=makeQuery(id+"F5.opPattern","COPY",BODY,{"derivedFrom":makeQuery(id+"F4.opExtrude","SWEPT_BODY",BODY,{"disambiguationData":[OSD([sQuery(id+"F3.wireOp",EDGE,"E9")])]}),"instanceName":"277"});
            var Q278;
            Q278=makeQuery(id+"F5.opPattern","COPY",BODY,{"derivedFrom":makeQuery(id+"F4.opExtrude","SWEPT_BODY",BODY,{"disambiguationData":[OSD([sQuery(id+"F3.wireOp",EDGE,"E9")])]}),"instanceName":"278"});
            var Q279;
            Q279=makeQuery(id+"F5.opPattern","COPY",BODY,{"derivedFrom":makeQuery(id+"F4.opExtrude","SWEPT_BODY",BODY,{"disambiguationData":[OSD([sQuery(id+"F3.wireOp",EDGE,"E9")])]}),"instanceName":"279"});
            var Q280;
            Q280=makeQuery(id+"F5.opPattern","COPY",BODY,{"derivedFrom":makeQuery(id+"F4.opExtrude","SWEPT_BODY",BODY,{"disambiguationData":[OSD([sQuery(id+"F3.wireOp",EDGE,"E9")])]}),"instanceName":"280"});
            var Q281;
            Q281=makeQuery(id+"F5.opPattern","COPY",BODY,{"derivedFrom":makeQuery(id+"F4.opExtrude","SWEPT_BODY",BODY,{"disambiguationData":[OSD([sQuery(id+"F3.wireOp",EDGE,"E9")])]}),"instanceName":"281"});
            var Q282;
            Q282=makeQuery(id+"F5.opPattern","COPY",BODY,{"derivedFrom":makeQuery(id+"F4.opExtrude","SWEPT_BODY",BODY,{"disambiguationData":[OSD([sQuery(id+"F3.wireOp",EDGE,"E9")])]}),"instanceName":"282"});
            var Q283;
            Q283=makeQuery(id+"F5.opPattern","COPY",BODY,{"derivedFrom":makeQuery(id+"F4.opExtrude","SWEPT_BODY",BODY,{"disambiguationData":[OSD([sQuery(id+"F3.wireOp",EDGE,"E9")])]}),"instanceName":"283"});
            var Q284;
            Q284=makeQuery(id+"F5.opPattern","COPY",BODY,{"derivedFrom":makeQuery(id+"F4.opExtrude","SWEPT_BODY",BODY,{"disambiguationData":[OSD([sQuery(id+"F3.wireOp",EDGE,"E9")])]}),"instanceName":"284"});
            var Q285;
            Q285=makeQuery(id+"F5.opPattern","COPY",BODY,{"derivedFrom":makeQuery(id+"F4.opExtrude","SWEPT_BODY",BODY,{"disambiguationData":[OSD([sQuery(id+"F3.wireOp",EDGE,"E9")])]}),"instanceName":"285"});
            var Q286;
            Q286=makeQuery(id+"F5.opPattern","COPY",BODY,{"derivedFrom":makeQuery(id+"F4.opExtrude","SWEPT_BODY",BODY,{"disambiguationData":[OSD([sQuery(id+"F3.wireOp",EDGE,"E9")])]}),"instanceName":"286"});
            var Q287;
            Q287=makeQuery(id+"F5.opPattern","COPY",BODY,{"derivedFrom":makeQuery(id+"F4.opExtrude","SWEPT_BODY",BODY,{"disambiguationData":[OSD([sQuery(id+"F3.wireOp",EDGE,"E9")])]}),"instanceName":"287"});
            var Q288;
            Q288=makeQuery(id+"F5.opPattern","COPY",BODY,{"derivedFrom":makeQuery(id+"F4.opExtrude","SWEPT_BODY",BODY,{"disambiguationData":[OSD([sQuery(id+"F3.wireOp",EDGE,"E9")])]}),"instanceName":"288"});
            var Q289;
            Q289=makeQuery(id+"F5.opPattern","COPY",BODY,{"derivedFrom":makeQuery(id+"F4.opExtrude","SWEPT_BODY",BODY,{"disambiguationData":[OSD([sQuery(id+"F3.wireOp",EDGE,"E9")])]}),"instanceName":"289"});
            var Q290;
            Q290=makeQuery(id+"F5.opPattern","COPY",BODY,{"derivedFrom":makeQuery(id+"F4.opExtrude","SWEPT_BODY",BODY,{"disambiguationData":[OSD([sQuery(id+"F3.wireOp",EDGE,"E9")])]}),"instanceName":"290"});
            var Q291;
            Q291=makeQuery(id+"F5.opPattern","COPY",BODY,{"derivedFrom":makeQuery(id+"F4.opExtrude","SWEPT_BODY",BODY,{"disambiguationData":[OSD([sQuery(id+"F3.wireOp",EDGE,"E9")])]}),"instanceName":"291"});
            var Q292;
            Q292=makeQuery(id+"F5.opPattern","COPY",BODY,{"derivedFrom":makeQuery(id+"F4.opExtrude","SWEPT_BODY",BODY,{"disambiguationData":[OSD([sQuery(id+"F3.wireOp",EDGE,"E9")])]}),"instanceName":"292"});
            var Q293;
            Q293=makeQuery(id+"F5.opPattern","COPY",BODY,{"derivedFrom":makeQuery(id+"F4.opExtrude","SWEPT_BODY",BODY,{"disambiguationData":[OSD([sQuery(id+"F3.wireOp",EDGE,"E9")])]}),"instanceName":"293"});
            var Q294;
            Q294=makeQuery(id+"F5.opPattern","COPY",BODY,{"derivedFrom":makeQuery(id+"F4.opExtrude","SWEPT_BODY",BODY,{"disambiguationData":[OSD([sQuery(id+"F3.wireOp",EDGE,"E9")])]}),"instanceName":"294"});
            var Q295;
            Q295=makeQuery(id+"F5.opPattern","COPY",BODY,{"derivedFrom":makeQuery(id+"F4.opExtrude","SWEPT_BODY",BODY,{"disambiguationData":[OSD([sQuery(id+"F3.wireOp",EDGE,"E9")])]}),"instanceName":"295"});
            var Q296;
            Q296=makeQuery(id+"F5.opPattern","COPY",BODY,{"derivedFrom":makeQuery(id+"F4.opExtrude","SWEPT_BODY",BODY,{"disambiguationData":[OSD([sQuery(id+"F3.wireOp",EDGE,"E9")])]}),"instanceName":"296"});
            var Q297;
            Q297=makeQuery(id+"F5.opPattern","COPY",BODY,{"derivedFrom":makeQuery(id+"F4.opExtrude","SWEPT_BODY",BODY,{"disambiguationData":[OSD([sQuery(id+"F3.wireOp",EDGE,"E9")])]}),"instanceName":"297"});
            var Q298;
            Q298=makeQuery(id+"F5.opPattern","COPY",BODY,{"derivedFrom":makeQuery(id+"F4.opExtrude","SWEPT_BODY",BODY,{"disambiguationData":[OSD([sQuery(id+"F3.wireOp",EDGE,"E9")])]}),"instanceName":"298"});
            var Q299;
            Q299=makeQuery(id+"F5.opPattern","COPY",BODY,{"derivedFrom":makeQuery(id+"F4.opExtrude","SWEPT_BODY",BODY,{"disambiguationData":[OSD([sQuery(id+"F3.wireOp",EDGE,"E9")])]}),"instanceName":"299"});
            var Q300;
            Q300=makeQuery(id+"F5.opPattern","COPY",BODY,{"derivedFrom":makeQuery(id+"F4.opExtrude","SWEPT_BODY",BODY,{"disambiguationData":[OSD([sQuery(id+"F3.wireOp",EDGE,"E9")])]}),"instanceName":"300"});
            var Q301;
            Q301=makeQuery(id+"F5.opPattern","COPY",BODY,{"derivedFrom":makeQuery(id+"F4.opExtrude","SWEPT_BODY",BODY,{"disambiguationData":[OSD([sQuery(id+"F3.wireOp",EDGE,"E9")])]}),"instanceName":"301"});
            var Q302;
            Q302=makeQuery(id+"F5.opPattern","COPY",BODY,{"derivedFrom":makeQuery(id+"F4.opExtrude","SWEPT_BODY",BODY,{"disambiguationData":[OSD([sQuery(id+"F3.wireOp",EDGE,"E9")])]}),"instanceName":"302"});
            var Q303;
            Q303=makeQuery(id+"F5.opPattern","COPY",BODY,{"derivedFrom":makeQuery(id+"F4.opExtrude","SWEPT_BODY",BODY,{"disambiguationData":[OSD([sQuery(id+"F3.wireOp",EDGE,"E9")])]}),"instanceName":"303"});
            var Q304;
            Q304=makeQuery(id+"F5.opPattern","COPY",BODY,{"derivedFrom":makeQuery(id+"F4.opExtrude","SWEPT_BODY",BODY,{"disambiguationData":[OSD([sQuery(id+"F3.wireOp",EDGE,"E9")])]}),"instanceName":"304"});
            var Q305;
            Q305=makeQuery(id+"F5.opPattern","COPY",BODY,{"derivedFrom":makeQuery(id+"F4.opExtrude","SWEPT_BODY",BODY,{"disambiguationData":[OSD([sQuery(id+"F3.wireOp",EDGE,"E9")])]}),"instanceName":"305"});
            var Q306;
            Q306=makeQuery(id+"F5.opPattern","COPY",BODY,{"derivedFrom":makeQuery(id+"F4.opExtrude","SWEPT_BODY",BODY,{"disambiguationData":[OSD([sQuery(id+"F3.wireOp",EDGE,"E9")])]}),"instanceName":"306"});
            var Q307;
            Q307=makeQuery(id+"F5.opPattern","COPY",BODY,{"derivedFrom":makeQuery(id+"F4.opExtrude","SWEPT_BODY",BODY,{"disambiguationData":[OSD([sQuery(id+"F3.wireOp",EDGE,"E9")])]}),"instanceName":"307"});
            var Q308;
            Q308=makeQuery(id+"F5.opPattern","COPY",BODY,{"derivedFrom":makeQuery(id+"F4.opExtrude","SWEPT_BODY",BODY,{"disambiguationData":[OSD([sQuery(id+"F3.wireOp",EDGE,"E9")])]}),"instanceName":"308"});
            var Q309;
            Q309=makeQuery(id+"F5.opPattern","COPY",BODY,{"derivedFrom":makeQuery(id+"F4.opExtrude","SWEPT_BODY",BODY,{"disambiguationData":[OSD([sQuery(id+"F3.wireOp",EDGE,"E9")])]}),"instanceName":"309"});
            var Q310;
            Q310=makeQuery(id+"F5.opPattern","COPY",BODY,{"derivedFrom":makeQuery(id+"F4.opExtrude","SWEPT_BODY",BODY,{"disambiguationData":[OSD([sQuery(id+"F3.wireOp",EDGE,"E9")])]}),"instanceName":"310"});
            var Q311;
            Q311=makeQuery(id+"F5.opPattern","COPY",BODY,{"derivedFrom":makeQuery(id+"F4.opExtrude","SWEPT_BODY",BODY,{"disambiguationData":[OSD([sQuery(id+"F3.wireOp",EDGE,"E9")])]}),"instanceName":"311"});
            var Q312;
            Q312=makeQuery(id+"F5.opPattern","COPY",BODY,{"derivedFrom":makeQuery(id+"F4.opExtrude","SWEPT_BODY",BODY,{"disambiguationData":[OSD([sQuery(id+"F3.wireOp",EDGE,"E9")])]}),"instanceName":"312"});
            var Q313;
            Q313=makeQuery(id+"F5.opPattern","COPY",BODY,{"derivedFrom":makeQuery(id+"F4.opExtrude","SWEPT_BODY",BODY,{"disambiguationData":[OSD([sQuery(id+"F3.wireOp",EDGE,"E9")])]}),"instanceName":"313"});
            var Q314;
            Q314=makeQuery(id+"F5.opPattern","COPY",BODY,{"derivedFrom":makeQuery(id+"F4.opExtrude","SWEPT_BODY",BODY,{"disambiguationData":[OSD([sQuery(id+"F3.wireOp",EDGE,"E9")])]}),"instanceName":"314"});
            var Q315;
            Q315=makeQuery(id+"F5.opPattern","COPY",BODY,{"derivedFrom":makeQuery(id+"F4.opExtrude","SWEPT_BODY",BODY,{"disambiguationData":[OSD([sQuery(id+"F3.wireOp",EDGE,"E9")])]}),"instanceName":"315"});
            var Q316;
            Q316=makeQuery(id+"F5.opPattern","COPY",BODY,{"derivedFrom":makeQuery(id+"F4.opExtrude","SWEPT_BODY",BODY,{"disambiguationData":[OSD([sQuery(id+"F3.wireOp",EDGE,"E9")])]}),"instanceName":"316"});
            var Q317;
            Q317=makeQuery(id+"F5.opPattern","COPY",BODY,{"derivedFrom":makeQuery(id+"F4.opExtrude","SWEPT_BODY",BODY,{"disambiguationData":[OSD([sQuery(id+"F3.wireOp",EDGE,"E9")])]}),"instanceName":"317"});
            var Q318;
            Q318=makeQuery(id+"F5.opPattern","COPY",BODY,{"derivedFrom":makeQuery(id+"F4.opExtrude","SWEPT_BODY",BODY,{"disambiguationData":[OSD([sQuery(id+"F3.wireOp",EDGE,"E9")])]}),"instanceName":"318"});
            var Q319;
            Q319=makeQuery(id+"F5.opPattern","COPY",BODY,{"derivedFrom":makeQuery(id+"F4.opExtrude","SWEPT_BODY",BODY,{"disambiguationData":[OSD([sQuery(id+"F3.wireOp",EDGE,"E9")])]}),"instanceName":"319"});
            var Q320;
            Q320=makeQuery(id+"F5.opPattern","COPY",BODY,{"derivedFrom":makeQuery(id+"F4.opExtrude","SWEPT_BODY",BODY,{"disambiguationData":[OSD([sQuery(id+"F3.wireOp",EDGE,"E9")])]}),"instanceName":"320"});
            var Q321;
            Q321=makeQuery(id+"F5.opPattern","COPY",BODY,{"derivedFrom":makeQuery(id+"F4.opExtrude","SWEPT_BODY",BODY,{"disambiguationData":[OSD([sQuery(id+"F3.wireOp",EDGE,"E9")])]}),"instanceName":"321"});
            var Q322;
            Q322=makeQuery(id+"F5.opPattern","COPY",BODY,{"derivedFrom":makeQuery(id+"F4.opExtrude","SWEPT_BODY",BODY,{"disambiguationData":[OSD([sQuery(id+"F3.wireOp",EDGE,"E9")])]}),"instanceName":"322"});
            var Q323;
            Q323=makeQuery(id+"F5.opPattern","COPY",BODY,{"derivedFrom":makeQuery(id+"F4.opExtrude","SWEPT_BODY",BODY,{"disambiguationData":[OSD([sQuery(id+"F3.wireOp",EDGE,"E9")])]}),"instanceName":"323"});
            var Q324;
            Q324=makeQuery(id+"F5.opPattern","COPY",BODY,{"derivedFrom":makeQuery(id+"F4.opExtrude","SWEPT_BODY",BODY,{"disambiguationData":[OSD([sQuery(id+"F3.wireOp",EDGE,"E9")])]}),"instanceName":"324"});
            var Q325;
            Q325=makeQuery(id+"F5.opPattern","COPY",BODY,{"derivedFrom":makeQuery(id+"F4.opExtrude","SWEPT_BODY",BODY,{"disambiguationData":[OSD([sQuery(id+"F3.wireOp",EDGE,"E9")])]}),"instanceName":"325"});
            var Q326;
            Q326=makeQuery(id+"F5.opPattern","COPY",BODY,{"derivedFrom":makeQuery(id+"F4.opExtrude","SWEPT_BODY",BODY,{"disambiguationData":[OSD([sQuery(id+"F3.wireOp",EDGE,"E9")])]}),"instanceName":"326"});
            var Q327;
            Q327=makeQuery(id+"F5.opPattern","COPY",BODY,{"derivedFrom":makeQuery(id+"F4.opExtrude","SWEPT_BODY",BODY,{"disambiguationData":[OSD([sQuery(id+"F3.wireOp",EDGE,"E9")])]}),"instanceName":"327"});
            var Q328;
            Q328=makeQuery(id+"F5.opPattern","COPY",BODY,{"derivedFrom":makeQuery(id+"F4.opExtrude","SWEPT_BODY",BODY,{"disambiguationData":[OSD([sQuery(id+"F3.wireOp",EDGE,"E9")])]}),"instanceName":"328"});
            var Q329;
            Q329=makeQuery(id+"F5.opPattern","COPY",BODY,{"derivedFrom":makeQuery(id+"F4.opExtrude","SWEPT_BODY",BODY,{"disambiguationData":[OSD([sQuery(id+"F3.wireOp",EDGE,"E9")])]}),"instanceName":"329"});
            var Q330;
            Q330=makeQuery(id+"F5.opPattern","COPY",BODY,{"derivedFrom":makeQuery(id+"F4.opExtrude","SWEPT_BODY",BODY,{"disambiguationData":[OSD([sQuery(id+"F3.wireOp",EDGE,"E9")])]}),"instanceName":"330"});
            var Q331;
            Q331=makeQuery(id+"F5.opPattern","COPY",BODY,{"derivedFrom":makeQuery(id+"F4.opExtrude","SWEPT_BODY",BODY,{"disambiguationData":[OSD([sQuery(id+"F3.wireOp",EDGE,"E9")])]}),"instanceName":"331"});
            var Q332;
            Q332=makeQuery(id+"F5.opPattern","COPY",BODY,{"derivedFrom":makeQuery(id+"F4.opExtrude","SWEPT_BODY",BODY,{"disambiguationData":[OSD([sQuery(id+"F3.wireOp",EDGE,"E9")])]}),"instanceName":"332"});
            var Q333;
            Q333=makeQuery(id+"F5.opPattern","COPY",BODY,{"derivedFrom":makeQuery(id+"F4.opExtrude","SWEPT_BODY",BODY,{"disambiguationData":[OSD([sQuery(id+"F3.wireOp",EDGE,"E9")])]}),"instanceName":"333"});
            var Q334;
            Q334=makeQuery(id+"F5.opPattern","COPY",BODY,{"derivedFrom":makeQuery(id+"F4.opExtrude","SWEPT_BODY",BODY,{"disambiguationData":[OSD([sQuery(id+"F3.wireOp",EDGE,"E9")])]}),"instanceName":"334"});
            var Q335;
            Q335=makeQuery(id+"F5.opPattern","COPY",BODY,{"derivedFrom":makeQuery(id+"F4.opExtrude","SWEPT_BODY",BODY,{"disambiguationData":[OSD([sQuery(id+"F3.wireOp",EDGE,"E9")])]}),"instanceName":"335"});
            var Q336;
            Q336=makeQuery(id+"F5.opPattern","COPY",BODY,{"derivedFrom":makeQuery(id+"F4.opExtrude","SWEPT_BODY",BODY,{"disambiguationData":[OSD([sQuery(id+"F3.wireOp",EDGE,"E9")])]}),"instanceName":"336"});
            var Q337;
            Q337=makeQuery(id+"F5.opPattern","COPY",BODY,{"derivedFrom":makeQuery(id+"F4.opExtrude","SWEPT_BODY",BODY,{"disambiguationData":[OSD([sQuery(id+"F3.wireOp",EDGE,"E9")])]}),"instanceName":"337"});
            var Q338;
            Q338=makeQuery(id+"F5.opPattern","COPY",BODY,{"derivedFrom":makeQuery(id+"F4.opExtrude","SWEPT_BODY",BODY,{"disambiguationData":[OSD([sQuery(id+"F3.wireOp",EDGE,"E9")])]}),"instanceName":"338"});
            var Q339;
            Q339=makeQuery(id+"F5.opPattern","COPY",BODY,{"derivedFrom":makeQuery(id+"F4.opExtrude","SWEPT_BODY",BODY,{"disambiguationData":[OSD([sQuery(id+"F3.wireOp",EDGE,"E9")])]}),"instanceName":"339"});
            var Q340;
            Q340=makeQuery(id+"F5.opPattern","COPY",BODY,{"derivedFrom":makeQuery(id+"F4.opExtrude","SWEPT_BODY",BODY,{"disambiguationData":[OSD([sQuery(id+"F3.wireOp",EDGE,"E9")])]}),"instanceName":"340"});
            var Q341;
            Q341=makeQuery(id+"F5.opPattern","COPY",BODY,{"derivedFrom":makeQuery(id+"F4.opExtrude","SWEPT_BODY",BODY,{"disambiguationData":[OSD([sQuery(id+"F3.wireOp",EDGE,"E9")])]}),"instanceName":"341"});
            var Q342;
            Q342=makeQuery(id+"F5.opPattern","COPY",BODY,{"derivedFrom":makeQuery(id+"F4.opExtrude","SWEPT_BODY",BODY,{"disambiguationData":[OSD([sQuery(id+"F3.wireOp",EDGE,"E9")])]}),"instanceName":"342"});
            var Q343;
            Q343=makeQuery(id+"F5.opPattern","COPY",BODY,{"derivedFrom":makeQuery(id+"F4.opExtrude","SWEPT_BODY",BODY,{"disambiguationData":[OSD([sQuery(id+"F3.wireOp",EDGE,"E9")])]}),"instanceName":"343"});
            var Q344;
            Q344=makeQuery(id+"F5.opPattern","COPY",BODY,{"derivedFrom":makeQuery(id+"F4.opExtrude","SWEPT_BODY",BODY,{"disambiguationData":[OSD([sQuery(id+"F3.wireOp",EDGE,"E9")])]}),"instanceName":"344"});
            var Q345;
            Q345=makeQuery(id+"F5.opPattern","COPY",BODY,{"derivedFrom":makeQuery(id+"F4.opExtrude","SWEPT_BODY",BODY,{"disambiguationData":[OSD([sQuery(id+"F3.wireOp",EDGE,"E9")])]}),"instanceName":"345"});
            var Q346;
            Q346=makeQuery(id+"F5.opPattern","COPY",BODY,{"derivedFrom":makeQuery(id+"F4.opExtrude","SWEPT_BODY",BODY,{"disambiguationData":[OSD([sQuery(id+"F3.wireOp",EDGE,"E9")])]}),"instanceName":"346"});
            var Q347;
            Q347=makeQuery(id+"F5.opPattern","COPY",BODY,{"derivedFrom":makeQuery(id+"F4.opExtrude","SWEPT_BODY",BODY,{"disambiguationData":[OSD([sQuery(id+"F3.wireOp",EDGE,"E9")])]}),"instanceName":"347"});
            var Q348;
            Q348=makeQuery(id+"F5.opPattern","COPY",BODY,{"derivedFrom":makeQuery(id+"F4.opExtrude","SWEPT_BODY",BODY,{"disambiguationData":[OSD([sQuery(id+"F3.wireOp",EDGE,"E9")])]}),"instanceName":"348"});
            var Q349;
            Q349=makeQuery(id+"F5.opPattern","COPY",BODY,{"derivedFrom":makeQuery(id+"F4.opExtrude","SWEPT_BODY",BODY,{"disambiguationData":[OSD([sQuery(id+"F3.wireOp",EDGE,"E9")])]}),"instanceName":"349"});
            var Q350;
            Q350=makeQuery(id+"F5.opPattern","COPY",BODY,{"derivedFrom":makeQuery(id+"F4.opExtrude","SWEPT_BODY",BODY,{"disambiguationData":[OSD([sQuery(id+"F3.wireOp",EDGE,"E9")])]}),"instanceName":"350"});
            var Q351;
            Q351=makeQuery(id+"F5.opPattern","COPY",BODY,{"derivedFrom":makeQuery(id+"F4.opExtrude","SWEPT_BODY",BODY,{"disambiguationData":[OSD([sQuery(id+"F3.wireOp",EDGE,"E9")])]}),"instanceName":"351"});
            var Q352;
            Q352=makeQuery(id+"F5.opPattern","COPY",BODY,{"derivedFrom":makeQuery(id+"F4.opExtrude","SWEPT_BODY",BODY,{"disambiguationData":[OSD([sQuery(id+"F3.wireOp",EDGE,"E9")])]}),"instanceName":"352"});
            var Q353;
            Q353=makeQuery(id+"F5.opPattern","COPY",BODY,{"derivedFrom":makeQuery(id+"F4.opExtrude","SWEPT_BODY",BODY,{"disambiguationData":[OSD([sQuery(id+"F3.wireOp",EDGE,"E9")])]}),"instanceName":"353"});
            var Q354;
            Q354=makeQuery(id+"F5.opPattern","COPY",BODY,{"derivedFrom":makeQuery(id+"F4.opExtrude","SWEPT_BODY",BODY,{"disambiguationData":[OSD([sQuery(id+"F3.wireOp",EDGE,"E9")])]}),"instanceName":"354"});
            var Q355;
            Q355=makeQuery(id+"F5.opPattern","COPY",BODY,{"derivedFrom":makeQuery(id+"F4.opExtrude","SWEPT_BODY",BODY,{"disambiguationData":[OSD([sQuery(id+"F3.wireOp",EDGE,"E9")])]}),"instanceName":"355"});
            var Q356;
            Q356=makeQuery(id+"F5.opPattern","COPY",BODY,{"derivedFrom":makeQuery(id+"F4.opExtrude","SWEPT_BODY",BODY,{"disambiguationData":[OSD([sQuery(id+"F3.wireOp",EDGE,"E9")])]}),"instanceName":"356"});
            var Q357;
            Q357=makeQuery(id+"F5.opPattern","COPY",BODY,{"derivedFrom":makeQuery(id+"F4.opExtrude","SWEPT_BODY",BODY,{"disambiguationData":[OSD([sQuery(id+"F3.wireOp",EDGE,"E9")])]}),"instanceName":"357"});
            var Q358;
            Q358=makeQuery(id+"F5.opPattern","COPY",BODY,{"derivedFrom":makeQuery(id+"F4.opExtrude","SWEPT_BODY",BODY,{"disambiguationData":[OSD([sQuery(id+"F3.wireOp",EDGE,"E9")])]}),"instanceName":"358"});
            var Q359;
            Q359=makeQuery(id+"F5.opPattern","COPY",BODY,{"derivedFrom":makeQuery(id+"F4.opExtrude","SWEPT_BODY",BODY,{"disambiguationData":[OSD([sQuery(id+"F3.wireOp",EDGE,"E9")])]}),"instanceName":"359"});
            var Q360;
            Q360=makeQuery(id+"F2.opRevolve","SWEPT_BODY",BODY,{"disambiguationData":[OSD([sQuery(id+"F1.wireOp",EDGE,"E0"),sQuery(id+"F1.wireOp",EDGE,"E1"),sQuery(id+"F1.wireOp",EDGE,"E2"),sQuery(id+"F1.wireOp",EDGE,"E3"),sQuery(id+"F1.wireOp",EDGE,"E4"),sQuery(id+"F1.wireOp",EDGE,"E5"),sQuery(id+"F1.wireOp",EDGE,"E6"),sQuery(id+"F1.wireOp",EDGE,"E7")])]});
            booleanBodies(context, id + "F6", {"operationType" : BooleanOperationType.SUBTRACTION, "tools" : qUnion([Q0, Q1, Q2, Q3, Q4, Q5, Q6, Q7, Q8, Q9, Q10, Q11, Q12, Q13, Q14, Q15, Q16, Q17, Q18, Q19, Q20, Q21, Q22, Q23, Q24, Q25, Q26, Q27, Q28, Q29, Q30, Q31, Q32, Q33, Q34, Q35, Q36, Q37, Q38, Q39, Q40, Q41, Q42, Q43, Q44, Q45, Q46, Q47, Q48, Q49, Q50, Q51, Q52, Q53, Q54, Q55, Q56, Q57, Q58, Q59, Q60, Q61, Q62, Q63, Q64, Q65, Q66, Q67, Q68, Q69, Q70, Q71, Q72, Q73, Q74, Q75, Q76, Q77, Q78, Q79, Q80, Q81, Q82, Q83, Q84, Q85, Q86, Q87, Q88, Q89, Q90, Q91, Q92, Q93, Q94, Q95, Q96, Q97, Q98, Q99, Q100, Q101, Q102, Q103, Q104, Q105, Q106, Q107, Q108, Q109, Q110, Q111, Q112, Q113, Q114, Q115, Q116, Q117, Q118, Q119, Q120, Q121, Q122, Q123, Q124, Q125, Q126, Q127, Q128, Q129, Q130, Q131, Q132, Q133, Q134, Q135, Q136, Q137, Q138, Q139, Q140, Q141, Q142, Q143, Q144, Q145, Q146, Q147, Q148, Q149, Q150, Q151, Q152, Q153, Q154, Q155, Q156, Q157, Q158, Q159, Q160, Q161, Q162, Q163, Q164, Q165, Q166, Q167, Q168, Q169, Q170, Q171, Q172, Q173, Q174, Q175, Q176, Q177, Q178, Q179, Q180, Q181, Q182, Q183, Q184, Q185, Q186, Q187, Q188, Q189, Q190, Q191, Q192, Q193, Q194, Q195, Q196, Q197, Q198, Q199, Q200, Q201, Q202, Q203, Q204, Q205, Q206, Q207, Q208, Q209, Q210, Q211, Q212, Q213, Q214, Q215, Q216, Q217, Q218, Q219, Q220, Q221, Q222, Q223, Q224, Q225, Q226, Q227, Q228, Q229, Q230, Q231, Q232, Q233, Q234, Q235, Q236, Q237, Q238, Q239, Q240, Q241, Q242, Q243, Q244, Q245, Q246, Q247, Q248, Q249, Q250, Q251, Q252, Q253, Q254, Q255, Q256, Q257, Q258, Q259, Q260, Q261, Q262, Q263, Q264, Q265, Q266, Q267, Q268, Q269, Q270, Q271, Q272, Q273, Q274, Q275, Q276, Q277, Q278, Q279, Q280, Q281, Q282, Q283, Q284, Q285, Q286, Q287, Q288, Q289, Q290, Q291, Q292, Q293, Q294, Q295, Q296, Q297, Q298, Q299, Q300, Q301, Q302, Q303, Q304, Q305, Q306, Q307, Q308, Q309, Q310, Q311, Q312, Q313, Q314, Q315, Q316, Q317, Q318, Q319, Q320, Q321, Q322, Q323, Q324, Q325, Q326, Q327, Q328, Q329, Q330, Q331, Q332, Q333, Q334, Q335, Q336, Q337, Q338, Q339, Q340, Q341, Q342, Q343, Q344, Q345, Q346, Q347, Q348, Q349, Q350, Q351, Q352, Q353, Q354, Q355, Q356, Q357, Q358, Q359]), "targets" : qUnion([Q360])});
        }
    });
